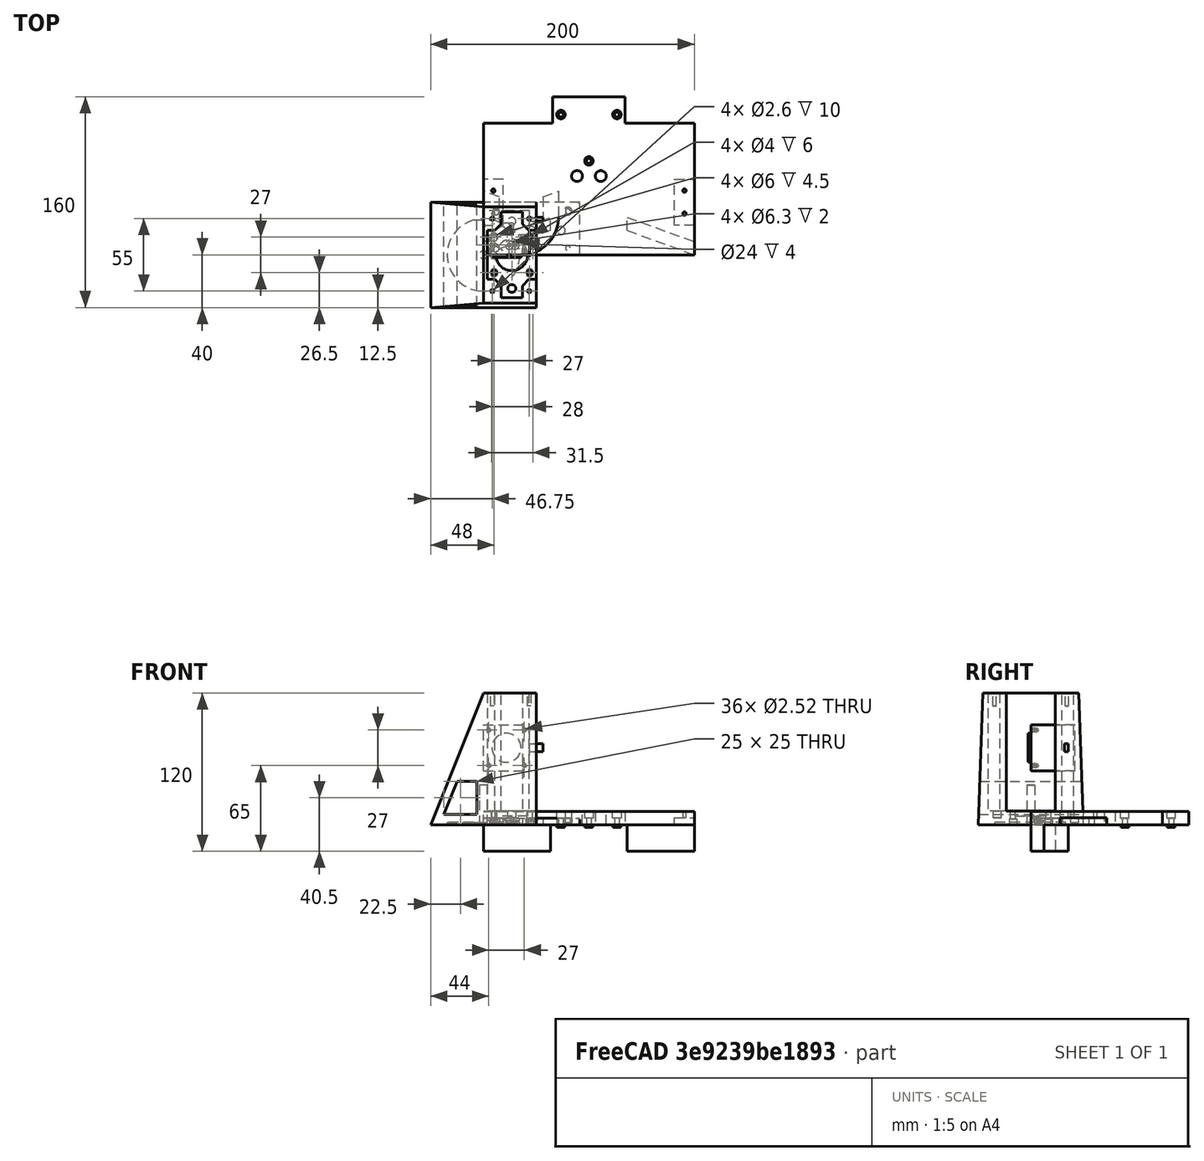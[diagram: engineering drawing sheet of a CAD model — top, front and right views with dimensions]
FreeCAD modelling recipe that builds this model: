
FCSTD DOCUMENT  (FreeCAD 1.0R39109 (Git))
Label: charging-station
License: All rights reserved
LicenseURL: http://en.wikipedia.org/wiki/All_rights_reserved
objects: Sketcher::SketchObject×37, PartDesign::Pocket×23, PartDesign::Pad×13, App::Link×9, App::FeaturePython×9, PartDesign::Body×8, PartDesign::Fillet×2, PartDesign::Hole×1, PartDesign::Chamfer×1, Assembly::JointGroup×1, Assembly::AssemblyObject×1
note: 202 computed .brp shape members not serialized (recipe doc carries the construction recipe); baked Part::Feature solids carry a one-line shape summary decoded from their .brp

FEATURE [Sketcher::SketchObject] Sketch
  ArcFitTolerance = 0
  AttachmentSupport = -> [XY_Plane]
  FullyConstrained = true
  MakeInternals = false
  MapMode = 5
  sketch-geometry (4):
    g0: LineSegment StartX=0 StartY=0 StartZ=0 EndX=160 EndY=0 EndZ=0
    g1: LineSegment StartX=160 StartY=0 StartZ=0 EndX=160 EndY=100 EndZ=0
    g2: LineSegment StartX=160 StartY=100 StartZ=0 EndX=0 EndY=100 EndZ=0
    g3: LineSegment StartX=0 StartY=100 StartZ=0 EndX=0 EndY=0 EndZ=0
  constraints (11):
    c: Coincident(g0,g1)
    c: Coincident(g1,g2)
    c: Coincident(g2,g3)
    c: Coincident(g3,g0)
    c: Horizontal(g0)
    c: Horizontal(g2)
    c: Vertical(g1)
    c: Vertical(g3)
    c: Coincident(g0,g-1)
    c: DistanceY(g1,g1) = 100
    c: DistanceX(g0,g0) = 160
FEATURE [PartDesign::Pad] Pad
  Direction = (0,0,1)
  Length = 10
  Length2 = 10
  Profile = -> Sketch
  ReferenceAxis = -> Sketch [N_Axis]
  Suppressed = false
  Type = 0
FEATURE [Sketcher::SketchObject] Sketch001
  ArcFitTolerance = 0
  AttachmentSupport = -> [Pad]
  ExternalGeometry = -> [Pad]
  FullyConstrained = true
  MakeInternals = false
  MapMode = 5
  Placement = pos=(0,0,0) rot=(1,0,0;3.14159rad)
  sketch-geometry (15):
    g0: LineSegment [constr] StartX=63.5 StartY=-33.1121 StartZ=0 EndX=96.5 EndY=-33.1121 EndZ=0
    g1: LineSegment StartX=0 StartY=-10 StartZ=0 EndX=0 EndY=0 EndZ=0
    g2: LineSegment [constr] StartX=63.5 StartY=-23.1121 StartZ=0 EndX=63.5 EndY=-33.1121 EndZ=0
    g3: LineSegment [constr] StartX=96.5 StartY=-33.1121 StartZ=0 EndX=96.5 EndY=-23.1121 EndZ=0
    g4: LineSegment StartX=160 StartY=0 StartZ=0 EndX=160 EndY=-10 EndZ=0
    g5: LineSegment StartX=51 StartY=-18.5625 StartZ=0 EndX=51 EndY=-28.5625 EndZ=0
    g6: LineSegment StartX=0 StartY=-10 StartZ=0 EndX=51 EndY=-28.5625 EndZ=0
    g7: LineSegment [constr] StartX=51 StartY=-28.5625 StartZ=0 EndX=63.5 EndY=-33.1121 EndZ=0
    g8: LineSegment [constr] StartX=63.5 StartY=-23.1121 StartZ=0 EndX=51 EndY=-18.5625 EndZ=0
    g9: LineSegment StartX=51 StartY=-18.5625 StartZ=0 EndX=0 EndY=0 EndZ=0
    g10: LineSegment StartX=109 StartY=-18.5625 StartZ=0 EndX=109 EndY=-28.5625 EndZ=0
    g11: LineSegment [constr] StartX=96.5 StartY=-23.1121 StartZ=0 EndX=109 EndY=-18.5625 EndZ=0
    g12: LineSegment StartX=109 StartY=-18.5625 StartZ=0 EndX=160 EndY=0 EndZ=0
    g13: LineSegment [constr] StartX=96.5 StartY=-33.1121 StartZ=0 EndX=109 EndY=-28.5625 EndZ=0
    g14: LineSegment StartX=109 StartY=-28.5625 StartZ=0 EndX=160 EndY=-10 EndZ=0
  constraints (40):
    c: DistanceX(g0,g0) = 33
    c: Horizontal(g0)
    c: Vertical(g3)
    c: Vertical(g4)
    c: Vertical(g2)
    c: Equal(g2,g3)
    c: DistanceY(g4,g4) = 10
    c: Coincident(g1,g-1)
    c: Vertical(g1)
    c: Vertical(g5)
    c: DistanceX(g5,g0) = 12.5
    c: Coincident(g1,g6)
    c: Coincident(g6,g5)
    c: Coincident(g6,g7)
    c: Coincident(g7,g2)
    c: Coincident(g2,g8)
    c: Coincident(g8,g5)
    c: Coincident(g8,g9)
    c: Coincident(g9,g1)
    c: Vertical(g10)
    c: Coincident(g3,g11)
    c: Coincident(g11,g10)
    c: Coincident(g11,g12)
    c: Coincident(g3,g13)
    c: Coincident(g13,g10)
    c: Coincident(g13,g14)
    c: Coincident(g14,g4)
    c: Equal(g13,g7)
    c: Coincident(g2,g0)
    c: Coincident(g3,g0)
    c: Parallel(g6,g9)
    c: Parallel(g14,g12)
    c: Parallel(g7,g8)
    c: Parallel(g13,g11)
    c: Parallel(g13,g14)
    c: Parallel(g7,g6)
    c: Angle(g-1,g12) = 0.349066
    c: Equal(g14,g6)
    c: Coincident(g12,g-3)
    c: Coincident(g4,g12)
FEATURE [Sketcher::SketchObject] Sketch002
  ArcFitTolerance = 0
  AttachmentSupport = -> [XY_Plane001]
  FullyConstrained = true
  MakeInternals = false
  MapMode = 5
  sketch-geometry (4):
    g0: LineSegment StartX=0 StartY=0 StartZ=0 EndX=35 EndY=0 EndZ=0
    g1: LineSegment StartX=35 StartY=0 StartZ=0 EndX=35 EndY=33.5 EndZ=0
    g2: LineSegment StartX=35 StartY=33.5 StartZ=0 EndX=0 EndY=33.5 EndZ=0
    g3: LineSegment StartX=0 StartY=33.5 StartZ=0 EndX=0 EndY=0 EndZ=0
  constraints (11):
    c: Coincident(g0,g1)
    c: Coincident(g1,g2)
    c: Coincident(g2,g3)
    c: Coincident(g3,g0)
    c: Horizontal(g0)
    c: Horizontal(g2)
    c: Vertical(g1)
    c: Vertical(g3)
    c: Coincident(g0,g-1)
    c: DistanceY(g1,g1) = 33.5
    c: DistanceX(g2,g2) = 35
FEATURE [PartDesign::Pad] Pad001
  Direction = (0,0,1)
  Length = 35
  Length2 = 10
  Profile = -> Sketch002
  ReferenceAxis = -> Sketch002 [N_Axis]
  Refine = true
  Suppressed = false
  Type = 0
FEATURE [Sketcher::SketchObject] Sketch003
  ArcFitTolerance = 0
  AttachmentSupport = -> [Pad001]
  ExternalGeometry = -> [Pad001]
  FullyConstrained = true
  MakeInternals = false
  MapMode = 5
  Placement = pos=(0,0,0) rot=(1,0,0;1.5708rad)
  sketch-geometry (4):
    g0: LineSegment [constr] StartX=0 StartY=0 StartZ=0 EndX=35 EndY=35 EndZ=0
    g1: LineSegment [constr] StartX=0 StartY=35 StartZ=0 EndX=35 EndY=0 EndZ=0
    g2: GeomPoint [constr] X=17.5 Y=17.5 Z=0
    g3: Circle CenterX=17.5 CenterY=17.5 CenterZ=0 NormalX=0 NormalY=0 NormalZ=1 AngleXU=0 Radius=11
  constraints (7):
    c: Coincident(g-1,g0)
    c: Coincident(g0,g-3)
    c: Coincident(g1,g-4)
    c: Coincident(g1,g-5)
    c: Symmetric(g1,g1,g2)
    c: Coincident(g3,g2)
    c: Diameter(g3) = 22
FEATURE [PartDesign::Pad] Pad002
  BaseFeature = -> Pad001
  Direction = (0,-1,2e-16)
  Length = 2
  Length2 = 10
  Profile = -> Sketch003
  ReferenceAxis = -> Sketch003 [N_Axis]
  Refine = true
  Suppressed = false
  Type = 0
FEATURE [Sketcher::SketchObject] Sketch004
  ArcFitTolerance = 0
  AttachmentSupport = -> [Pad002]
  ExternalGeometry = -> [Pad002]
  FullyConstrained = true
  MakeInternals = false
  MapMode = 5
  Placement = pos=(0,0,0) rot=(1,0,0;1.5708rad)
  sketch-geometry (6):
    g0: LineSegment [constr] StartX=35 StartY=35 StartZ=0 EndX=0 EndY=0 EndZ=0
    g1: LineSegment [constr] StartX=0 StartY=35 StartZ=0 EndX=35 EndY=0 EndZ=0
    g2: Circle CenterX=31 CenterY=31 CenterZ=0 NormalX=0 NormalY=0 NormalZ=1 AngleXU=0 Radius=1.5
    g3: Circle CenterX=4 CenterY=31 CenterZ=0 NormalX=0 NormalY=0 NormalZ=1 AngleXU=0 Radius=1.5
    g4: Circle CenterX=31 CenterY=4 CenterZ=0 NormalX=0 NormalY=0 NormalZ=1 AngleXU=0 Radius=1.5
    g5: Circle CenterX=4 CenterY=4 CenterZ=0 NormalX=0 NormalY=0 NormalZ=1 AngleXU=0 Radius=1.5
  constraints (16):
    c: Coincident(g-7,g0)
    c: Coincident(g0,g-1)
    c: Coincident(g-9,g1)
    c: Coincident(g1,g-8)
    c: PointOnObject(g2,g0)
    c: PointOnObject(g3,g1)
    c: PointOnObject(g4,g1)
    c: PointOnObject(g5,g0)
    c: DistanceX(g2,g0) = 4
    c: DistanceX(g4,g1) = 4
    c: DistanceX(g0,g5) = 4
    c: DistanceX(g1,g3) = 4
    c: Diameter(g2) = 3
    c: Diameter(g4) = 3
    c: Diameter(g5) = 3
    c: Diameter(g3) = 3
FEATURE [PartDesign::Hole] Hole
  BaseFeature = -> Pad002
  CustomThreadClearance = 0
  Depth = 5
  DepthType = 0
  Diameter = 2.52
  DrillForDepth = false
  DrillPoint = 1
  DrillPointAngle = 118
  HoleCutCountersinkAngle = 90
  HoleCutCustomValues = false
  HoleCutDepth = 0
  HoleCutDiameter = 6
  HoleCutType = 0
  ModelThread = true
  Profile = -> Sketch004
  Refine = true
  Suppressed = false
  Tapered = false
  TaperedAngle = 90
  ThreadClass = 0
  ThreadDepth = 5
  ThreadDepthType = 0
  ThreadDirection = 0
  ThreadFit = 0
  ThreadSize = 9
  ThreadType = 1
  Threaded = true
  UseCustomThreadClearance = false
FEATURE [Sketcher::SketchObject] Sketch005
  ArcFitTolerance = 0
  AttachmentSupport = -> [Hole]
  ExternalGeometry = -> [Hole]
  FullyConstrained = true
  MakeInternals = false
  MapMode = 5
  Placement = pos=(35,0,0) rot=(0.57735,0.57735,0.57735;2.0944rad)
  sketch-geometry (9):
    g0: LineSegment [constr] StartX=33.5 StartY=35 StartZ=0 EndX=33.5 EndY=20.5 EndZ=0
    g1: LineSegment [constr] StartX=33.5 StartY=20.5 StartZ=0 EndX=33.5 EndY=14.5 EndZ=0
    g2: LineSegment [constr] StartX=33.5 StartY=14.5 StartZ=0 EndX=33.5 EndY=0 EndZ=0
    g3: LineSegment [constr] StartX=33.5 StartY=20.5 StartZ=0 EndX=28.5 EndY=20.5 EndZ=0
    g4: LineSegment [constr] StartX=33.5 StartY=14.5 StartZ=0 EndX=28.5 EndY=14.5 EndZ=0
    g5: LineSegment StartX=28.5 StartY=20.5 StartZ=0 EndX=25.5 EndY=20.5 EndZ=0
    g6: LineSegment StartX=25.5 StartY=20.5 StartZ=0 EndX=25.5 EndY=14.5 EndZ=0
    g7: LineSegment StartX=25.5 StartY=14.5 StartZ=0 EndX=28.5 EndY=14.5 EndZ=0
    g8: LineSegment StartX=28.5 StartY=14.5 StartZ=0 EndX=28.5 EndY=20.5 EndZ=0
  constraints (24):
    c: Coincident(g-4,g0)
    c: PointOnObject(g0,g-3)
    c: Coincident(g0,g1)
    c: PointOnObject(g1,g-3)
    c: Coincident(g1,g2)
    c: Coincident(g2,g-3)
    c: Equal(g2,g0)
    c: DistanceY(g1,g1) = 6
    c: Coincident(g0,g3)
    c: Horizontal(g3)
    c: Coincident(g1,g4)
    c: Horizontal(g4)
    c: Coincident(g5,g6)
    c: Coincident(g6,g7)
    c: Coincident(g7,g8)
    c: Coincident(g8,g5)
    c: Horizontal(g5)
    c: Horizontal(g7)
    c: Vertical(g6)
    c: Vertical(g8)
    c: Coincident(g5,g3)
    c: Coincident(g7,g4)
    c: DistanceX(g5,g5) = 3
    c: DistanceX(g3,g3) = 5
FEATURE [Sketcher::SketchObject] Sketch006
  ArcFitTolerance = 0
  AttachmentSupport = -> [XY_Plane002]
  FullyConstrained = true
  MakeInternals = false
  MapMode = 5
  sketch-geometry (2):
    g0: ArcOfCircle CenterX=0 CenterY=0 CenterZ=0 NormalX=0 NormalY=0 NormalZ=1 AngleXU=0 Radius=27.5 StartAngle=1.8413 EndAngle=7.58348
    g1: LineSegment StartX=-7.34847 StartY=26.5 StartZ=0 EndX=7.34847 EndY=26.5 EndZ=0
  constraints (6):
    c: Coincident(g0,g-1)
    c: Diameter(g0) = 55
    c: Horizontal(g1)
    c: Distance(g0,g1) = 26.5
    c: Coincident(g0,g1)
    c: Coincident(g0,g1)
FEATURE [PartDesign::Pad] Pad004
  Direction = (0,0,1)
  Length = 2
  Length2 = 10
  Profile = -> Sketch006
  ReferenceAxis = -> Sketch006 [N_Axis]
  Refine = true
  Suppressed = false
  Type = 0
FEATURE [PartDesign::Body] Body002  label="dezibot"
  AllowCompound = false
  Group = -> [Sketch006,Pad004]
  Origin = -> Origin002
  Tip = -> Pad004
FEATURE [App::Link] Body003  label="Beam"
  LinkPlacement = pos=(-173.162,-33.5765,-80.1161) rot=(0,0,1;0rad)
  LinkedObject = -> Body
  Placement = pos=(-173.162,-33.5765,-80.1161) rot=(0,0,1;0rad)
FEATURE [App::Link] Body004  label="BaseLeft"
  LinkPlacement = pos=(-213.899,29.7686,-94.7418) rot=(0,0,1;0rad)
  LinkedObject = -> Body006
  Placement = pos=(-213.899,29.7686,-94.7418) rot=(0,0,1;0rad)
FEATURE [Sketcher::SketchObject] Sketch007
  ArcFitTolerance = 0
  AttachmentSupport = -> [XY_Plane004]
  FullyConstrained = true
  MakeInternals = false
  MapMode = 5
  sketch-geometry (8):
    g0: LineSegment StartX=-40 StartY=40 StartZ=0 EndX=-40 EndY=-40 EndZ=0
    g1: LineSegment StartX=-40 StartY=-40 StartZ=0 EndX=40 EndY=-40 EndZ=0
    g2: LineSegment StartX=40 StartY=-40 StartZ=0 EndX=40 EndY=40 EndZ=0
    g3: LineSegment StartX=40 StartY=40 StartZ=0 EndX=-40 EndY=40 EndZ=0
    g4: LineSegment [constr] StartX=40 StartY=-40 StartZ=0 EndX=0 EndY=0 EndZ=0
    g5: LineSegment [constr] StartX=0 StartY=0 StartZ=0 EndX=-40 EndY=40 EndZ=0
    g6: LineSegment [constr] StartX=-40 StartY=-40 StartZ=0 EndX=0 EndY=0 EndZ=0
    g7: LineSegment [constr] StartX=0 StartY=0 StartZ=0 EndX=40 EndY=40 EndZ=0
  constraints (20):
    c: Coincident(g0,g1)
    c: Coincident(g1,g2)
    c: Coincident(g2,g3)
    c: Coincident(g3,g0)
    c: Vertical(g0)
    c: Vertical(g2)
    c: Horizontal(g1)
    c: Horizontal(g3)
    c: DistanceY(g2,g2) = 80
    c: DistanceX(g1,g1) = 80
    c: Coincident(g1,g4)
    c: Coincident(g4,g-1)
    c: Coincident(g4,g5)
    c: Coincident(g5,g0)
    c: Equal(g5,g4)
    c: Coincident(g0,g6)
    c: Coincident(g6,g4)
    c: Coincident(g6,g7)
    c: Coincident(g7,g2)
    c: Equal(g7,g6)
FEATURE [PartDesign::Pad] Pad005
  Direction = (0,0,1)
  Length = 100
  Length2 = 10
  Profile = -> Sketch007
  ReferenceAxis = -> Sketch007 [N_Axis]
  Refine = true
  Suppressed = false
  Type = 0
FEATURE [Sketcher::SketchObject] Sketch008
  ArcFitTolerance = 0
  AttachmentSupport = -> [Pad005]
  ExternalGeometry = -> [Pad005]
  FullyConstrained = true
  MakeInternals = false
  MapMode = 5
  Placement = pos=(0,-40,0) rot=(1,0,0;1.5708rad)
  sketch-geometry (10):
    g0: LineSegment StartX=-40 StartY=0 StartZ=0 EndX=0 EndY=100 EndZ=0
    g1: LineSegment [constr] StartX=0 StartY=100 StartZ=0 EndX=40 EndY=100 EndZ=0
    g2: LineSegment [constr] StartX=40 StartY=100 StartZ=0 EndX=40 EndY=0 EndZ=0
    g3: LineSegment [constr] StartX=40 StartY=0 StartZ=0 EndX=-40 EndY=0 EndZ=0
    g4: LineSegment StartX=0 StartY=100 StartZ=0 EndX=-40 EndY=100 EndZ=0
    g5: LineSegment StartX=-40 StartY=100 StartZ=0 EndX=-40 EndY=0 EndZ=0
    g6: LineSegment StartX=-30 StartY=8 StartZ=0 EndX=-5 EndY=8 EndZ=0
    g7: LineSegment StartX=-5 StartY=8 StartZ=0 EndX=-5 EndY=33 EndZ=0
    g8: LineSegment StartX=-20 StartY=33 StartZ=0 EndX=-30 EndY=8 EndZ=0
    g9: LineSegment StartX=-5 StartY=33 StartZ=0 EndX=-20 EndY=33 EndZ=0
  constraints (26):
    c: Coincident(g-4,g0)
    c: Coincident(g0,g1)
    c: Coincident(g1,g-5)
    c: Horizontal(g1)
    c: Coincident(g1,g2)
    c: Coincident(g2,g-5)
    c: Coincident(g2,g3)
    c: Coincident(g3,g0)
    c: DistanceX(g1,g1) = 40
    c: Coincident(g0,g4)
    c: Horizontal(g4)
    c: Coincident(g4,g5)
    c: Coincident(g5,g0)
    c: Vertical(g5)
    c: Horizontal(g6)
    c: Coincident(g6,g7)
    c: Vertical(g7)
    c: Coincident(g8,g6)
    c: DistanceX(g6,g-1) = 5
    c: DistanceY(g-1,g6) = 8
    c: DistanceX(g0,g6) = 10
    c: Parallel(g8,g0)
    c: Horizontal(g9)
    c: DistanceY(g6,g9) = 25
    c: Coincident(g7,g9)
    c: Coincident(g8,g9)
FEATURE [PartDesign::Pocket] Pocket001
  BaseFeature = -> Pad005
  Direction = (0,1,-2e-16)
  Length = 5
  Length2 = 5
  Profile = -> Sketch008
  ReferenceAxis = -> Sketch008 [N_Axis]
  Refine = true
  Suppressed = false
  Type = 1
FEATURE [Sketcher::SketchObject] Sketch009
  ArcFitTolerance = 0
  AttachmentSupport = -> [Pocket001]
  ExternalGeometry = -> [Pocket001]
  FullyConstrained = true
  MakeInternals = false
  MapMode = 5
  Placement = pos=(40,0,0) rot=(0.57735,0.57735,0.57735;2.0944rad)
  sketch-geometry (6):
    g0: LineSegment StartX=-36.5 StartY=100 StartZ=0 EndX=-40 EndY=0 EndZ=0
    g1: LineSegment StartX=40 StartY=0 StartZ=0 EndX=36.5 EndY=100 EndZ=0
    g2: LineSegment StartX=-36.5 StartY=100 StartZ=0 EndX=-40 EndY=100 EndZ=0
    g3: LineSegment StartX=-40 StartY=100 StartZ=0 EndX=-40 EndY=0 EndZ=0
    g4: LineSegment StartX=36.5 StartY=100 StartZ=0 EndX=40 EndY=100 EndZ=0
    g5: LineSegment StartX=40 StartY=100 StartZ=0 EndX=40 EndY=0 EndZ=0
  constraints (13):
    c: DistanceX(g0,g1) = 73
    c: Symmetric(g0,g1,g-2)
    c: Coincident(g-3,g1)
    c: PointOnObject(g1,g-4)
    c: Coincident(g0,g-3)
    c: Coincident(g0,g2)
    c: Coincident(g2,g-4)
    c: Coincident(g2,g3)
    c: Coincident(g3,g0)
    c: Coincident(g1,g4)
    c: Coincident(g4,g-4)
    c: Coincident(g4,g5)
    c: Coincident(g5,g1)
FEATURE [PartDesign::Pocket] Pocket002
  BaseFeature = -> Pocket001
  Direction = (-1,0,0)
  Length = 5
  Length2 = 5
  Profile = -> Sketch009
  ReferenceAxis = -> Sketch009 [N_Axis]
  Refine = true
  Suppressed = false
  Type = 1
FEATURE [App::FeaturePython] GroundedJoint001  # Assembly grounded joint (typed FeaturePython)
  ObjectToGround = -> Body004
  Placement = pos=(-213.899,29.7686,-94.7418) rot=(0,0,1;0rad)
FEATURE [Sketcher::SketchObject] Sketch011
  ArcFitTolerance = 0
  AttachmentSupport = -> [Pocket002]
  ExternalGeometry = -> [Pocket002]
  FullyConstrained = true
  MakeInternals = false
  MapMode = 5
  Placement = pos=(40,0,0) rot=(0.57735,0.57735,0.57735;2.0944rad)
  sketch-geometry (5):
    g0: LineSegment StartX=-18.5 StartY=10.5 StartZ=0 EndX=18.5 EndY=10.5 EndZ=0
    g1: LineSegment StartX=18.5 StartY=10.5 StartZ=0 EndX=18.5 EndY=1671.43 EndZ=0
    g2: LineSegment StartX=18.5 StartY=1671.43 StartZ=0 EndX=-18.5 EndY=1671.43 EndZ=0
    g3: LineSegment StartX=-18.5 StartY=1671.43 StartZ=0 EndX=-18.5 EndY=10.5 EndZ=0
    g4: GeomPoint X=0 Y=1671.43 Z=0
  constraints (13):
    c: Coincident(g0,g1)
    c: Coincident(g1,g2)
    c: Coincident(g2,g3)
    c: Coincident(g3,g0)
    c: Horizontal(g0)
    c: Horizontal(g2)
    c: Vertical(g1)
    c: Vertical(g3)
    c: PointOnObject(g1,g-3)
    c: DistanceX(g2,g2) = 37
    c: Symmetric(g2,g2,g4)
    c: PointOnObject(g4,g-2)
    c: DistanceY(g-1,g0) = 10.5
FEATURE [PartDesign::Pocket] Pocket003
  BaseFeature = -> Pocket002
  Direction = (-1,0,0)
  Length = 37
  Length2 = 5
  Profile = -> Sketch011
  ReferenceAxis = -> Sketch011 [N_Axis]
  Refine = true
  Suppressed = false
  Type = 0
FEATURE [Sketcher::SketchObject] Sketch012
  ArcFitTolerance = 0
  AttachmentSupport = -> [Pocket003]
  ExternalGeometry = -> [Pocket003]
  FullyConstrained = true
  MakeInternals = false
  MapMode = 5
  Placement = pos=(0,0,10.5) rot=(0,0,1;0rad)
  sketch-geometry (4):
    g0: Circle CenterX=21.5 CenterY=0 CenterZ=0 NormalX=0 NormalY=0 NormalZ=1 AngleXU=0 Radius=12
    g1: LineSegment [constr] StartX=3 StartY=18.5 StartZ=0 EndX=40 EndY=-18.5 EndZ=0
    g2: LineSegment [constr] StartX=40 StartY=18.5 StartZ=0 EndX=3 EndY=-18.5 EndZ=0
    g3: GeomPoint [constr] X=21.5 Y=0 Z=0
  constraints (7):
    c: Diameter(g0) = 24
    c: Coincident(g1,g-3)
    c: Coincident(g1,g-5)
    c: Coincident(g2,g-6)
    c: Coincident(g2,g-4)
    c: Symmetric(g1,g1,g3)
    c: Coincident(g3,g0)
FEATURE [PartDesign::Pocket] Pocket004
  BaseFeature = -> Pocket003
  Direction = (0,0,-1)
  Length = 4
  Length2 = 5
  Profile = -> Sketch012
  ReferenceAxis = -> Sketch012 [N_Axis]
  Refine = true
  Suppressed = false
  Type = 0
FEATURE [Sketcher::SketchObject] Sketch013
  ArcFitTolerance = 0
  AttachmentSupport = -> [Pocket004]
  ExternalGeometry = -> [Pocket004]
  FullyConstrained = true
  MakeInternals = false
  MapMode = 5
  Placement = pos=(0,0,10.5) rot=(0,0,1;0rad)
  sketch-geometry (20):
    g0: LineSegment [constr] StartX=3 StartY=18.5 StartZ=0 EndX=3 EndY=13.5 EndZ=0
    g1: LineSegment [constr] StartX=3 StartY=13.5 StartZ=0 EndX=8 EndY=13.5 EndZ=0
    g2: LineSegment [constr] StartX=8 StartY=13.5 StartZ=0 EndX=8 EndY=18.5 EndZ=0
    g3: LineSegment [constr] StartX=8 StartY=18.5 StartZ=0 EndX=3 EndY=18.5 EndZ=0
    g4: LineSegment [constr] StartX=35 StartY=13.5 StartZ=0 EndX=40 EndY=13.5 EndZ=0
    g5: LineSegment [constr] StartX=40 StartY=13.5 StartZ=0 EndX=40 EndY=18.5 EndZ=0
    g6: LineSegment [constr] StartX=40 StartY=18.5 StartZ=0 EndX=35 EndY=18.5 EndZ=0
    g7: LineSegment [constr] StartX=35 StartY=18.5 StartZ=0 EndX=35 EndY=13.5 EndZ=0
    g8: LineSegment [constr] StartX=3 StartY=-18.5 StartZ=0 EndX=8 EndY=-18.5 EndZ=0
    g9: LineSegment [constr] StartX=8 StartY=-18.5 StartZ=0 EndX=8 EndY=-13.5 EndZ=0
    g10: LineSegment [constr] StartX=8 StartY=-13.5 StartZ=0 EndX=3 EndY=-13.5 EndZ=0
    g11: LineSegment [constr] StartX=3 StartY=-13.5 StartZ=0 EndX=3 EndY=-18.5 EndZ=0
    g12: LineSegment [constr] StartX=35 StartY=-13.5 StartZ=0 EndX=35 EndY=-18.5 EndZ=0
    g13: LineSegment [constr] StartX=35 StartY=-18.5 StartZ=0 EndX=40 EndY=-18.5 EndZ=0
    g14: LineSegment [constr] StartX=40 StartY=-18.5 StartZ=0 EndX=40 EndY=-13.5 EndZ=0
    g15: LineSegment [constr] StartX=40 StartY=-13.5 StartZ=0 EndX=35 EndY=-13.5 EndZ=0
    g16: Circle CenterX=8 CenterY=13.5 CenterZ=0 NormalX=0 NormalY=0 NormalZ=1 AngleXU=0 Radius=2
    g17: Circle CenterX=35 CenterY=13.5 CenterZ=0 NormalX=0 NormalY=0 NormalZ=1 AngleXU=0 Radius=2
    g18: Circle CenterX=35 CenterY=-13.5 CenterZ=0 NormalX=0 NormalY=0 NormalZ=1 AngleXU=0 Radius=2
    g19: Circle CenterX=8 CenterY=-13.5 CenterZ=0 NormalX=0 NormalY=0 NormalZ=1 AngleXU=0 Radius=2
  constraints (52):
    c: Coincident(g0,g1)
    c: Coincident(g1,g2)
    c: Coincident(g2,g3)
    c: Coincident(g3,g0)
    c: Vertical(g0)
    c: Vertical(g2)
    c: Horizontal(g1)
    c: Horizontal(g3)
    c: Coincident(g0,g-4)
    c: Equal(g2,g1)
    c: DistanceY(g2,g2) = 5
    c: Coincident(g4,g5)
    c: Coincident(g5,g6)
    c: Coincident(g6,g7)
    c: Coincident(g7,g4)
    c: Horizontal(g4)
    c: Horizontal(g6)
    c: Vertical(g5)
    c: Vertical(g7)
    c: Coincident(g8,g9)
    c: Coincident(g9,g10)
    c: Coincident(g10,g11)
    c: Coincident(g11,g8)
    c: Horizontal(g8)
    c: Horizontal(g10)
    c: Vertical(g9)
    c: Vertical(g11)
    c: Coincident(g12,g13)
    c: Coincident(g13,g14)
    c: Coincident(g14,g15)
    c: Coincident(g15,g12)
    c: Vertical(g12)
    c: Vertical(g14)
    c: Horizontal(g13)
    c: Horizontal(g15)
    c: Equal(g7,g2)
    c: Equal(g4,g2)
    c: Coincident(g5,g-6)
    c: Coincident(g8,g-5)
    c: Equal(g10,g1)
    c: Equal(g10,g9)
    c: Equal(g12,g2)
    c: Equal(g15,g1)
    c: Coincident(g13,g-6)
    c: Coincident(g16,g1)
    c: Diameter(g16) = 4
    c: Coincident(g17,g4)
    c: Coincident(g18,g12)
    c: Coincident(g19,g9)
    c: Equal(g16,g17)
    c: Equal(g17,g18)
    c: Equal(g18,g19)
FEATURE [PartDesign::Pocket] Pocket005
  BaseFeature = -> Pocket004
  Direction = (0,0,-1)
  Length = 5
  Length2 = 5
  Profile = -> Sketch013
  ReferenceAxis = -> Sketch013 [N_Axis]
  Refine = true
  Suppressed = false
  Type = 1
FEATURE [Sketcher::SketchObject] Sketch014
  ArcFitTolerance = 0
  AttachmentSupport = -> [Pocket005]
  ExternalGeometry = -> [Pocket005]
  FullyConstrained = true
  MakeInternals = false
  MapMode = 5
  Placement = pos=(0,0,0) rot=(1,0,0;3.14159rad)
  sketch-geometry (4):
    g0: Circle CenterX=8 CenterY=13.5 CenterZ=0 NormalX=0 NormalY=0 NormalZ=1 AngleXU=0 Radius=3
    g1: Circle CenterX=35 CenterY=13.5 CenterZ=0 NormalX=0 NormalY=0 NormalZ=1 AngleXU=0 Radius=3
    g2: Circle CenterX=35 CenterY=-13.5 CenterZ=0 NormalX=0 NormalY=0 NormalZ=1 AngleXU=0 Radius=3
    g3: Circle CenterX=8 CenterY=-13.5 CenterZ=0 NormalX=0 NormalY=0 NormalZ=1 AngleXU=0 Radius=3
  constraints (8):
    c: Coincident(g0,g-3)
    c: Coincident(g1,g-4)
    c: Coincident(g2,g-5)
    c: Coincident(g3,g-6)
    c: Diameter(g0) = 6
    c: Equal(g0,g1)
    c: Equal(g1,g2)
    c: Equal(g2,g3)
FEATURE [App::Link] Body005  label="BaseRight"
  LinkPlacement = pos=(67.4324,29.1063,-94.7418) rot=(0,0,1;3.14159rad)
  LinkedObject = -> Body006
  Placement = pos=(67.4324,29.1063,-94.7418) rot=(0,0,1;3.14159rad)
FEATURE [App::FeaturePython] GroundedJoint  # Assembly grounded joint (typed FeaturePython)
  ObjectToGround = -> Body005
  Placement = pos=(67.4324,29.1063,-94.7418) rot=(0,0,1;3.14159rad)
FEATURE [Sketcher::SketchObject] Sketch019
  ArcFitTolerance = 0
  AttachmentSupport = -> [XY_Plane005]
  FullyConstrained = true
  MakeInternals = false
  MapMode = 5
  sketch-geometry (4):
    g0: LineSegment StartX=0 StartY=0 StartZ=0 EndX=73 EndY=0 EndZ=0
    g1: LineSegment StartX=73 StartY=0 StartZ=0 EndX=73 EndY=40 EndZ=0
    g2: LineSegment StartX=73 StartY=40 StartZ=0 EndX=0 EndY=40 EndZ=0
    g3: LineSegment StartX=0 StartY=40 StartZ=0 EndX=0 EndY=0 EndZ=0
  constraints (11):
    c: Coincident(g0,g1)
    c: Coincident(g1,g2)
    c: Coincident(g2,g3)
    c: Coincident(g3,g0)
    c: Horizontal(g0)
    c: Horizontal(g2)
    c: Vertical(g1)
    c: Vertical(g3)
    c: Coincident(g0,g-1)
    c: DistanceY(g1,g1) = 40
    c: DistanceX(g2,g2) = 73
FEATURE [PartDesign::Pad] Pad006
  Direction = (0,0,1)
  Length = 5
  Length2 = 10
  Profile = -> Sketch019
  ReferenceAxis = -> Sketch019 [N_Axis]
  Refine = true
  Suppressed = false
  Type = 0
FEATURE [Sketcher::SketchObject] Sketch020
  ArcFitTolerance = 0
  AttachmentSupport = -> [Pad006]
  ExternalGeometry = -> [Pad006]
  FullyConstrained = true
  MakeInternals = false
  MapMode = 5
  Placement = pos=(0,0,5) rot=(0,0,1;0rad)
  sketch-geometry (35):
    g0: LineSegment [constr] StartX=0 StartY=0 StartZ=0 EndX=18 EndY=0 EndZ=0
    g1: LineSegment [constr] StartX=18 StartY=0 StartZ=0 EndX=18 EndY=10.5 EndZ=0
    g2: LineSegment [constr] StartX=18 StartY=10.5 StartZ=0 EndX=0 EndY=10.5 EndZ=0
    g3: LineSegment [constr] StartX=0 StartY=10.5 StartZ=0 EndX=0 EndY=0 EndZ=0
    g4: LineSegment [constr] StartX=0 StartY=40 StartZ=0 EndX=0 EndY=26.5 EndZ=0
    g5: LineSegment [constr] StartX=0 StartY=26.5 StartZ=0 EndX=18 EndY=26.5 EndZ=0
    g6: LineSegment [constr] StartX=18 StartY=26.5 StartZ=0 EndX=18 EndY=37 EndZ=0
    g7: LineSegment [constr] StartX=18 StartY=40 StartZ=0 EndX=0 EndY=40 EndZ=0
    g8: LineSegment [constr] StartX=73 StartY=40 StartZ=0 EndX=55 EndY=40 EndZ=0
    g9: LineSegment [constr] StartX=55 StartY=37 StartZ=0 EndX=55 EndY=26.5 EndZ=0
    g10: LineSegment [constr] StartX=55 StartY=26.5 StartZ=0 EndX=73 EndY=26.5 EndZ=0
    g11: LineSegment [constr] StartX=73 StartY=26.5 StartZ=0 EndX=73 EndY=40 EndZ=0
    g12: LineSegment [constr] StartX=73 StartY=0 StartZ=0 EndX=73 EndY=10.5 EndZ=0
    g13: LineSegment [constr] StartX=73 StartY=10.5 StartZ=0 EndX=55 EndY=10.5 EndZ=0
    g14: LineSegment [constr] StartX=55 StartY=10.5 StartZ=0 EndX=55 EndY=0 EndZ=0
    g15: LineSegment [constr] StartX=55 StartY=0 StartZ=0 EndX=73 EndY=0 EndZ=0
    g16: Circle CenterX=14 CenterY=18.5 CenterZ=0 NormalX=0 NormalY=0 NormalZ=1 AngleXU=0 Radius=3
    g17: Circle CenterX=59 CenterY=18.5 CenterZ=0 NormalX=0 NormalY=0 NormalZ=1 AngleXU=0 Radius=3
    g18: Circle CenterX=36.5 CenterY=18.5 CenterZ=0 NormalX=0 NormalY=0 NormalZ=1 AngleXU=0 Radius=3
    g19: Circle CenterX=9 CenterY=33.25 CenterZ=0 NormalX=0 NormalY=0 NormalZ=1 AngleXU=0 Radius=1.75
    g20: Circle CenterX=64 CenterY=33.25 CenterZ=0 NormalX=0 NormalY=0 NormalZ=1 AngleXU=0 Radius=1.75
    g21: Circle CenterX=64 CenterY=5.25 CenterZ=0 NormalX=0 NormalY=0 NormalZ=1 AngleXU=0 Radius=1.75
    g22: Circle CenterX=9 CenterY=5.25 CenterZ=0 NormalX=0 NormalY=0 NormalZ=1 AngleXU=0 Radius=1.75
    g23: LineSegment [constr] StartX=0 StartY=26.5 StartZ=0 EndX=0 EndY=10.5 EndZ=0
    g24: LineSegment [constr] StartX=0 StartY=10.5 StartZ=0 EndX=10 EndY=10.5 EndZ=0
    g25: LineSegment [constr] StartX=10 StartY=10.5 StartZ=0 EndX=10 EndY=26.5 EndZ=0
    g26: LineSegment [constr] StartX=10 StartY=26.5 StartZ=0 EndX=0 EndY=26.5 EndZ=0
    g27: LineSegment [constr] StartX=73 StartY=10.5 StartZ=0 EndX=73 EndY=26.5 EndZ=0
    g28: LineSegment [constr] StartX=73 StartY=26.5 StartZ=0 EndX=63 EndY=26.5 EndZ=0
    g29: LineSegment [constr] StartX=63 StartY=26.5 StartZ=0 EndX=63 EndY=10.5 EndZ=0
    g30: LineSegment [constr] StartX=63 StartY=10.5 StartZ=0 EndX=73 EndY=10.5 EndZ=0
    g31: LineSegment [constr] StartX=18 StartY=40 StartZ=0 EndX=18 EndY=37 EndZ=0
    g32: LineSegment [constr] StartX=18 StartY=37 StartZ=0 EndX=55 EndY=37 EndZ=0
    g33: LineSegment [constr] StartX=55 StartY=37 StartZ=0 EndX=55 EndY=40 EndZ=0
    g34: LineSegment [constr] StartX=55 StartY=40 StartZ=0 EndX=18 EndY=40 EndZ=0
  constraints (92):
    c: Coincident(g0,g1)
    c: Coincident(g1,g2)
    c: Coincident(g2,g3)
    c: Coincident(g3,g0)
    c: Horizontal(g0)
    c: Horizontal(g2)
    c: Vertical(g1)
    c: Vertical(g3)
    c: Coincident(g0,g-1)
    c: Coincident(g4,g5)
    c: Coincident(g5,g6)
    c: Vertical(g4)
    c: Vertical(g6)
    c: Horizontal(g5)
    c: Horizontal(g7)
    c: Coincident(g9,g10)
    c: Coincident(g10,g11)
    c: Coincident(g11,g8)
    c: Horizontal(g8)
    c: Horizontal(g10)
    c: Vertical(g9)
    c: Vertical(g11)
    c: Coincident(g8,g-5)
    c: Coincident(g12,g13)
    c: Coincident(g13,g14)
    c: Coincident(g14,g15)
    c: Coincident(g15,g12)
    c: Vertical(g12)
    c: Vertical(g14)
    c: Horizontal(g13)
    c: Horizontal(g15)
    c: Coincident(g12,g-6)
    c: DistanceY(g2,g4) = 16
    c: DistanceX(g-1,g0) = 18
    c: Symmetric(g25,g1,g16)
    c: Symmetric(g9,g29,g17)
    c: Symmetric(g5,g13,g18)
    c: Diameter(g18) = 6
    c: Diameter(g16) = 6
    c: Equal(g16,g17)
    c: Symmetric(g13,g12,g21)
    c: Diameter(g19) = 3.5
    c: Coincident(g23,g24)
    c: Coincident(g24,g25)
    c: Coincident(g25,g26)
    c: Coincident(g26,g23)
    c: Vertical(g23)
    c: Vertical(g25)
    c: Horizontal(g24)
    c: Horizontal(g26)
    c: Coincident(g23,g4)
    c: PointOnObject(g24,g2)
    c: DistanceX(g24,g1) = 8
    c: Coincident(g27,g28)
    c: Coincident(g28,g29)
    c: Coincident(g29,g30)
    c: Coincident(g30,g27)
    c: Vertical(g27)
    c: Vertical(g29)
    c: Horizontal(g28)
    c: Horizontal(g30)
    c: Coincident(g27,g12)
    c: PointOnObject(g28,g10)
    c: DistanceX(g13,g29) = 8
    c: Coincident(g31,g32)
    c: Coincident(g32,g33)
    c: Coincident(g33,g34)
    c: Coincident(g34,g31)
    c: Vertical(g31)
    c: Vertical(g33)
    c: Horizontal(g32)
    c: Coincident(g31,g7)
    c: Coincident(g-4,g7)
    c: Coincident(g4,g7)
    c: Distance(g32,g8) = 3
    c: DistanceY(g5,g31) = 10.5
    c: DistanceY(g5,g7) = 13.5
    c: Symmetric(g5,g4,g19)
    c: Symmetric(g0,g1,g22)
    c: Symmetric(g9,g8,g20)
    c: Equal(g19,g22)
    c: Equal(g22,g21)
    c: Equal(g21,g20)
    c: Coincident(g9,g32)
    c: Equal(g6,g9)
    c: Equal(g14,g1)
    c: Equal(g1,g6)
    c: Coincident(g6,g31)
    c: Equal(g5,g10)
    c: Equal(g10,g13)
    c: Equal(g13,g2)
    c: Coincident(g8,g33)
FEATURE [PartDesign::Pocket] Pocket011
  BaseFeature = -> Pad006
  Direction = (0,0,-1)
  Length = 5
  Length2 = 5
  Profile = -> Sketch020
  ReferenceAxis = -> Sketch020 [N_Axis]
  Refine = true
  Suppressed = false
  Type = 2
FEATURE [Sketcher::SketchObject] Sketch021
  ArcFitTolerance = 0
  AttachmentSupport = -> [Pocket011]
  ExternalGeometry = -> [Pocket011]
  FullyConstrained = true
  MakeInternals = false
  MapMode = 5
  Placement = pos=(0,0,5) rot=(0,0,1;0rad)
  sketch-geometry (4):
    g0: Circle CenterX=36.5 CenterY=18.5 CenterZ=0 NormalX=0 NormalY=0 NormalZ=1 AngleXU=0 Radius=3
    g1: Circle CenterX=9 CenterY=5.25 CenterZ=0 NormalX=0 NormalY=0 NormalZ=1 AngleXU=0 Radius=3
    g2: Circle CenterX=64 CenterY=33.25 CenterZ=0 NormalX=0 NormalY=0 NormalZ=1 AngleXU=0 Radius=3
    g3: Circle CenterX=9 CenterY=33.25 CenterZ=0 NormalX=0 NormalY=0 NormalZ=1 AngleXU=0 Radius=3
  constraints (8):
    c: Coincident(g1,g-3)
    c: Coincident(g2,g-4)
    c: Diameter(g0) = 6
    c: Equal(g0,g2)
    c: Equal(g2,g3)
    c: Equal(g3,g1)
    c: Coincident(g3,g-5)
    c: Coincident(g0,g-6)
FEATURE [PartDesign::Pocket] Pocket012
  BaseFeature = -> Pocket011
  Direction = (0,0,-1)
  Length = 3.5
  Length2 = 5
  Profile = -> Sketch021
  ReferenceAxis = -> Sketch021 [N_Axis]
  Refine = true
  Suppressed = false
  Type = 0
FEATURE [PartDesign::Fillet] Fillet
  Base = -> Pocket012 [Edge10,Edge19,Edge7,Edge4]
  BaseFeature = -> Pocket012
  Radius = 1
  Refine = true
  SupportTransform = false
  Suppressed = false
  UseAllEdges = false
FEATURE [App::Link] base_top  label="BaseTopLeft"
  LinkPlacement = pos=(33.25,-64,0) rot=(0,0,1;1.5708rad)
  LinkedObject = -> Body007
  Placement = pos=(33.25,-64,0) rot=(0,0,1;1.5708rad)
FEATURE [Sketcher::SketchObject] Sketch023
  ArcFitTolerance = 0
  AttachmentSupport = -> [Fillet]
  ExternalGeometry = -> [Fillet]
  FullyConstrained = true
  MakeInternals = false
  MapMode = 5
  Placement = pos=(0,0,5) rot=(0,0,1;0rad)
  sketch-geometry (5):
    g0: LineSegment [constr] StartX=36.5 StartY=1 StartZ=0 EndX=36.5 EndY=4 EndZ=0
    g1: LineSegment StartX=36.5 StartY=4 StartZ=0 EndX=38.5 EndY=7 EndZ=0
    g2: LineSegment StartX=38.5 StartY=7 StartZ=0 EndX=34.5 EndY=7 EndZ=0
    g3: LineSegment StartX=34.5 StartY=7 StartZ=0 EndX=36.5 EndY=4 EndZ=0
    g4: LineSegment [constr] StartX=36.5 StartY=7 StartZ=0 EndX=36.5 EndY=4 EndZ=0
  constraints (13):
    c: Coincident(g1,g2)
    c: Horizontal(g2)
    c: Coincident(g2,g3)
    c: Coincident(g3,g1)
    c: DistanceX(g2,g2) = 4
    c: Vertical(g0)
    c: Coincident(g1,g0)
    c: DistanceY(g0,g0) = 3
    c: Symmetric(g-3,g-3,g0)
    c: Symmetric(g2,g2,g4)
    c: Coincident(g4,g0)
    c: Vertical(g4)
    c: DistanceY(g0,g1) = 3
FEATURE [PartDesign::Pocket] Pocket014
  BaseFeature = -> Fillet
  Direction = (0,0,-1)
  Length = 1
  Length2 = 5
  Profile = -> Sketch023
  ReferenceAxis = -> Sketch023 [N_Axis]
  Refine = true
  Suppressed = false
  Type = 0
FEATURE [PartDesign::Body] Body007  label="base-top"
  AllowCompound = false
  Group = -> [Sketch019,Pad006,Sketch020,Pocket011,Sketch021,Pocket012,Fillet,Sketch023,Pocket014]
  Origin = -> Origin005
  Tip = -> Pocket014
FEATURE [PartDesign::Pad] Pad003  label="cable"
  BaseFeature = -> Hole
  Direction = (1,0,0)
  Length = 10
  Length2 = 10
  Profile = -> Sketch005
  ReferenceAxis = -> Sketch005 [N_Axis]
  Refine = true
  Suppressed = false
  Type = 0
FEATURE [PartDesign::Body] Body001  label="stepper-motor"
  AllowCompound = false
  Group = -> [Sketch002,Pad001,Sketch003,Pad002,Sketch004,Hole,Sketch005,Pad003]
  Origin = -> Origin001
  Placement = pos=(0,0,41) rot=(0,0,1;0rad)
  Tip = -> Pad003
FEATURE [PartDesign::Pocket] Pocket006
  BaseFeature = -> Pocket005
  Direction = (0,0,1)
  Length = 4.5
  Length2 = 5
  Profile = -> Sketch014
  ReferenceAxis = -> Sketch014 [N_Axis]
  Refine = true
  Suppressed = false
  Type = 0
FEATURE [Sketcher::SketchObject] Sketch016
  ArcFitTolerance = 0
  AttachmentSupport = -> [Pocket006]
  ExternalGeometry = -> [Pocket006]
  FullyConstrained = true
  MakeInternals = false
  MapMode = 5
  Placement = pos=(0,18.5,0) rot=(1,0,0;1.5708rad)
  sketch-geometry (6):
    g0: LineSegment StartX=13.5 StartY=100 StartZ=0 EndX=13.5 EndY=10.5 EndZ=0
    g1: LineSegment StartX=13.5 StartY=10.5 StartZ=0 EndX=29.5 EndY=10.5 EndZ=0
    g2: LineSegment StartX=29.5 StartY=10.5 StartZ=0 EndX=29.5 EndY=100 EndZ=0
    g3: LineSegment [constr] StartX=3 StartY=100 StartZ=0 EndX=13.5 EndY=100 EndZ=0
    g4: LineSegment [constr] StartX=29.5 StartY=100 StartZ=0 EndX=40 EndY=100 EndZ=0
    g5: LineSegment StartX=13.5 StartY=100 StartZ=0 EndX=29.5 EndY=100 EndZ=0
  constraints (16):
    c: Coincident(g0,g1)
    c: Coincident(g1,g2)
    c: Vertical(g0)
    c: Vertical(g2)
    c: Horizontal(g1)
    c: Equal(g4,g3)
    c: DistanceX(g0,g2) = 16
    c: Coincident(g2,g4)
    c: Coincident(g3,g0)
    c: Horizontal(g3)
    c: Coincident(g0,g5)
    c: Coincident(g5,g2)
    c: Coincident(g3,g-3)
    c: Coincident(g4,g-3)
    c: PointOnObject(g2,g-3)
    c: PointOnObject(g1,g-4)
FEATURE [PartDesign::Pocket] Pocket008
  BaseFeature = -> Pocket006
  Direction = (0,1,-2e-16)
  Length = 14
  Length2 = 5
  Profile = -> Sketch016
  ReferenceAxis = -> Sketch016 [N_Axis]
  Refine = true
  Suppressed = false
  Type = 0
FEATURE [Sketcher::SketchObject] Sketch024
  ArcFitTolerance = 0
  AttachmentSupport = -> [Pocket008]
  ExternalGeometry = -> [Pocket008]
  FullyConstrained = true
  MakeInternals = false
  MapMode = 5
  Placement = pos=(0,-18.5,0) rot=(0,0.707107,0.707107;3.14159rad)
  sketch-geometry (6):
    g0: LineSegment StartX=-29.5 StartY=10.5 StartZ=0 EndX=-13.5 EndY=10.5 EndZ=0
    g1: LineSegment StartX=-13.5 StartY=10.5 StartZ=0 EndX=-13.5 EndY=100 EndZ=0
    g2: LineSegment StartX=-13.5 StartY=100 StartZ=0 EndX=-29.5 EndY=100 EndZ=0
    g3: LineSegment StartX=-29.5 StartY=100 StartZ=0 EndX=-29.5 EndY=10.5 EndZ=0
    g4: LineSegment [constr] StartX=-40 StartY=100 StartZ=0 EndX=-29.5 EndY=100 EndZ=0
    g5: LineSegment [constr] StartX=-13.5 StartY=100 StartZ=0 EndX=-3 EndY=100 EndZ=0
  constraints (16):
    c: Coincident(g2,g3)
    c: Coincident(g3,g0)
    c: Horizontal(g0)
    c: Horizontal(g2)
    c: Vertical(g1)
    c: Vertical(g3)
    c: PointOnObject(g1,g-3)
    c: DistanceX(g2,g2) = 16
    c: PointOnObject(g0,g-5)
    c: Coincident(g1,g2)
    c: Coincident(g1,g0)
    c: Coincident(g-3,g4)
    c: Coincident(g4,g2)
    c: Coincident(g1,g5)
    c: Coincident(g5,g-4)
    c: Equal(g5,g4)
FEATURE [PartDesign::Pocket] Pocket015
  BaseFeature = -> Pocket008
  Direction = (0,-1,2e-16)
  Length = 14
  Length2 = 5
  Profile = -> Sketch024
  ReferenceAxis = -> Sketch024 [N_Axis]
  Refine = true
  Suppressed = false
  Type = 0
FEATURE [Sketcher::SketchObject] Sketch018
  ArcFitTolerance = 0
  AttachmentSupport = -> [Pocket015]
  ExternalGeometry = -> [Pocket015]
  FullyConstrained = true
  MakeInternals = false
  MapMode = 5
  Placement = pos=(0,0,10.5) rot=(0,0,1;0rad)
  sketch-geometry (4):
    g0: LineSegment [constr] StartX=13.5 StartY=-18.5 StartZ=0 EndX=29.5 EndY=-32.5 EndZ=0
    g1: LineSegment [constr] StartX=13.5 StartY=18.5 StartZ=0 EndX=29.5 EndY=32.5 EndZ=0
    g2: Circle CenterX=21.5 CenterY=-25.5 CenterZ=0 NormalX=0 NormalY=0 NormalZ=1 AngleXU=0 Radius=3
    g3: Circle CenterX=21.5 CenterY=25.5 CenterZ=0 NormalX=0 NormalY=0 NormalZ=1 AngleXU=0 Radius=3
  constraints (8):
    c: Symmetric(g0,g0,g2)
    c: Diameter(g2) = 6
    c: Symmetric(g1,g1,g3)
    c: Equal(g3,g2)
    c: Coincident(g1,g-5)
    c: Coincident(g1,g-4)
    c: Coincident(g0,g-3)
    c: Coincident(g0,g-6)
FEATURE [PartDesign::Pocket] Pocket010
  BaseFeature = -> Pocket015
  Direction = (0,0,-1)
  Length = 5
  Length2 = 5
  Profile = -> Sketch018
  ReferenceAxis = -> Sketch018 [N_Axis]
  Refine = true
  Suppressed = false
  Type = 0
FEATURE [Sketcher::SketchObject] Sketch022
  ArcFitTolerance = 0
  AttachmentSupport = -> [Pocket010]
  ExternalGeometry = -> [Pocket010]
  FullyConstrained = true
  MakeInternals = false
  MapMode = 5
  Placement = pos=(0,0,100) rot=(0,0,1;0rad)
  sketch-geometry (8):
    g0: LineSegment [constr] StartX=13.5 StartY=18.5 StartZ=0 EndX=0 EndY=36.5 EndZ=0
    g1: LineSegment [constr] StartX=0 StartY=-36.5 StartZ=0 EndX=13.5 EndY=-18.5 EndZ=0
    g2: LineSegment [constr] StartX=29.5 StartY=-18.5 StartZ=0 EndX=40 EndY=-36.5 EndZ=0
    g3: LineSegment [constr] StartX=29.5 StartY=18.5 StartZ=0 EndX=40 EndY=36.5 EndZ=0
    g4: Circle CenterX=6.75 CenterY=27.5 CenterZ=0 NormalX=0 NormalY=0 NormalZ=1 AngleXU=0 Radius=1.3
    g5: Circle CenterX=34.75 CenterY=27.5 CenterZ=0 NormalX=0 NormalY=0 NormalZ=1 AngleXU=0 Radius=1.3
    g6: Circle CenterX=6.75 CenterY=-27.5 CenterZ=0 NormalX=0 NormalY=0 NormalZ=1 AngleXU=0 Radius=1.3
    g7: Circle CenterX=34.75 CenterY=-27.5 CenterZ=0 NormalX=0 NormalY=0 NormalZ=1 AngleXU=0 Radius=1.3
  constraints (16):
    c: Coincident(g1,g-8)
    c: Coincident(g1,g-9)
    c: Coincident(g2,g-9)
    c: Coincident(g2,g-10)
    c: Symmetric(g2,g2,g7)
    c: Symmetric(g1,g1,g6)
    c: Coincident(g0,g-12)
    c: Coincident(g0,g-13)
    c: Symmetric(g0,g0,g4)
    c: Symmetric(g3,g3,g5)
    c: Coincident(g3,g-11)
    c: Coincident(g3,g-13)
    c: Equal(g7,g6)
    c: Equal(g6,g4)
    c: Equal(g4,g5)
    c: Diameter(g4) = 2.6
FEATURE [PartDesign::Pocket] Pocket013
  BaseFeature = -> Pocket010
  Direction = (0,0,-1)
  Length = 10
  Length2 = 5
  Profile = -> Sketch022
  ReferenceAxis = -> Sketch022 [N_Axis]
  Refine = true
  Suppressed = false
  Type = 0
FEATURE [Sketcher::SketchObject] Sketch025
  ArcFitTolerance = 0
  AttachmentSupport = -> [XY_Plane006]
  FullyConstrained = true
  MakeInternals = false
  MapMode = 5
  sketch-geometry (8):
    g0: LineSegment [constr] StartX=0 StartY=0 StartZ=0 EndX=57 EndY=0 EndZ=0
    g1: LineSegment [constr] StartX=57 StartY=0 StartZ=0 EndX=57 EndY=57 EndZ=0
    g2: LineSegment [constr] StartX=57 StartY=57 StartZ=0 EndX=0 EndY=57 EndZ=0
    g3: LineSegment [constr] StartX=0 StartY=57 StartZ=0 EndX=0 EndY=0 EndZ=0
    g4: LineSegment StartX=0 StartY=28.5 StartZ=0 EndX=0 EndY=57 EndZ=0
    g5: LineSegment StartX=0 StartY=57 StartZ=0 EndX=57 EndY=57 EndZ=0
    g6: ArcOfCircle CenterX=28.5 CenterY=28.5 CenterZ=0 NormalX=0 NormalY=0 NormalZ=1 AngleXU=0 Radius=28.5 StartAngle=3.14159 EndAngle=6.28319
    g7: LineSegment StartX=57 StartY=57 StartZ=0 EndX=57 EndY=28.5 EndZ=0
  constraints (22):
    c: Coincident(g0,g1)
    c: Coincident(g1,g2)
    c: Coincident(g2,g3)
    c: Coincident(g3,g0)
    c: Horizontal(g0)
    c: Horizontal(g2)
    c: Vertical(g1)
    c: Coincident(g0,g-1)
    c: DistanceX(g2,g2) = 57
    c: Equal(g1,g2)
    c: Symmetric(g3,g3,g4)
    c: Coincident(g4,g2)
    c: Vertical(g4)
    c: Coincident(g4,g5)
    c: Horizontal(g5)
    c: Coincident(g6,g4)
    c: Tangent(g6,g0)
    c: Coincident(g5,g7)
    c: PointOnObject(g7,g1)
    c: Vertical(g7)
    c: Coincident(g6,g7)
    c: Equal(g7,g4)
FEATURE [PartDesign::Pad] Pad007
  Direction = (0,0,1)
  Length = 5
  Length2 = 10
  Profile = -> Sketch025
  ReferenceAxis = -> Sketch025 [N_Axis]
  Refine = true
  Suppressed = false
  Type = 0
FEATURE [Sketcher::SketchObject] Sketch026
  ArcFitTolerance = 0
  AttachmentSupport = -> [Pad007]
  ExternalGeometry = -> [Pad007]
  FullyConstrained = true
  MakeInternals = false
  MapMode = 5
  Placement = pos=(0,0,5) rot=(0,0,1;0rad)
  sketch-geometry (22):
    g0: ArcOfCircle [constr] CenterX=28.5 CenterY=28.5 CenterZ=0 NormalX=0 NormalY=0 NormalZ=1 AngleXU=0 Radius=27.5 StartAngle=1.8413 EndAngle=7.58348
    g1: LineSegment [constr] StartX=21.1515 StartY=55 StartZ=0 EndX=35.8485 EndY=55 EndZ=0
    g2: LineSegment [constr] StartX=28.5 StartY=55 StartZ=0 EndX=28.5 EndY=1 EndZ=0
    g3: GeomPoint [constr] X=28.5 Y=15 Z=0
    g4: GeomPoint [constr] X=28.5 Y=24 Z=0
    g5: LineSegment StartX=22.5 StartY=15 StartZ=0 EndX=34.5 EndY=15 EndZ=0
    g6: LineSegment StartX=12 StartY=24 StartZ=0 EndX=22.5 EndY=24 EndZ=0
    g7: LineSegment StartX=45 StartY=24 StartZ=0 EndX=45 EndY=44 EndZ=0
    g8: LineSegment StartX=45 StartY=57 StartZ=0 EndX=12 EndY=57 EndZ=0
    g9: LineSegment StartX=22.5 StartY=15 StartZ=0 EndX=22.5 EndY=24 EndZ=0
    g10: LineSegment StartX=34.5 StartY=15 StartZ=0 EndX=34.5 EndY=24 EndZ=0
    g11: LineSegment [constr] StartX=0 StartY=28.5 StartZ=0 EndX=56 EndY=28.5 EndZ=0
    g12: LineSegment StartX=34.5 StartY=24 StartZ=0 EndX=45 EndY=24 EndZ=0
    g13: LineSegment StartX=12 StartY=57 StartZ=0 EndX=-23.7172 EndY=57 EndZ=0
    g14: LineSegment StartX=45 StartY=57 StartZ=0 EndX=80.7172 EndY=57 EndZ=0
    g15: LineSegment StartX=-23.7172 StartY=57 StartZ=0 EndX=12 EndY=44 EndZ=0
    g16: LineSegment StartX=80.7172 StartY=57 StartZ=0 EndX=45 EndY=44 EndZ=0
    g17: LineSegment [constr] StartX=45 StartY=44 StartZ=0 EndX=12 EndY=44 EndZ=0
    g18: LineSegment StartX=12 StartY=44 StartZ=0 EndX=12 EndY=24 EndZ=0
    g19: LineSegment [constr] StartX=12 StartY=57 StartZ=0 EndX=12 EndY=44 EndZ=0
    g20: LineSegment [constr] StartX=45 StartY=44 StartZ=0 EndX=45 EndY=57 EndZ=0
    g21: GeomPoint [constr] X=0 Y=48.3676 Z=0
  constraints (63):
    c: Horizontal(g1)
    c: Symmetric(g1,g1,g2)
    c: PointOnObject(g2,g0)
    c: Vertical(g2)
    c: DistanceY(g2,g2) = 54
    c: Coincident(g0,g1)
    c: Coincident(g0,g1)
    c: Radius(g0) = 27.5
    c: PointOnObject(g3,g2)
    c: DistanceY(g2,g3) = 14
    c: PointOnObject(g4,g2)
    c: DistanceY(g2,g4) = 23
    c: Horizontal(g5)
    c: Coincident(g12,g7)
    c: Coincident(g18,g6)
    c: Horizontal(g6)
    c: Horizontal(g8)
    c: Vertical(g7)
    c: PointOnObject(g4,g6)
    c: Coincident(g5,g9)
    c: Vertical(g9)
    c: Coincident(g5,g10)
    c: PointOnObject(g10,g6)
    c: Vertical(g10)
    c: PointOnObject(g11,g-3)
    c: PointOnObject(g11,g0)
    c: Horizontal(g11)
    c: PointOnObject(g0,g11)
    c: Distance(g11,g7) = 11
    c: Coincident(g6,g9)
    c: Equal(g12,g6)
    c: Symmetric(g5,g5,g3)
    c: Horizontal(g12)
    c: Coincident(g12,g10)
    c: DistanceX(g5,g5) = 12
    c: Coincident(g8,g13)
    c: Horizontal(g13)
    c: Coincident(g8,g14)
    c: Horizontal(g14)
    c: Angle(g15,g13) = 0.349066
    c: DistanceY(g6,g15) = 20
    c: Coincident(g15,g13)
    c: Equal(g13,g14)
    c: Coincident(g14,g16)
    c: Coincident(g16,g17)
    c: Coincident(g17,g15)
    c: Horizontal(g17)
    c: Coincident(g7,g16)
    c: Coincident(g18,g15)
    c: Vertical(g18)
    c: Coincident(g8,g19)
    c: Coincident(g19,g15)
    c: Coincident(g7,g20)
    c: Coincident(g20,g8)
    c: Vertical(g20)
    c: Vertical(g19)
    c: Coincident(g0,g-4)
    c: PointOnObject(g8,g-5)
    c: PointOnObject(g21,g15)
    c: PointOnObject(g21,g-2)
    c: DistanceY(g9,g9) = 9
    c: DistanceX(g21,g15) = 12
    c: DistanceX(g17,g17) = 33
FEATURE [PartDesign::Pocket] Pocket016
  BaseFeature = -> Pad007
  Direction = (0,0,-1)
  Length = 5
  Length2 = 5
  Profile = -> Sketch026
  ReferenceAxis = -> Sketch026 [N_Axis]
  Refine = true
  Suppressed = false
  Type = 2
FEATURE [PartDesign::Pad] Pad008
  BaseFeature = -> Pad
  Direction = (0,0,-1)
  Length = 20
  Length2 = 10
  Profile = -> Sketch001
  ReferenceAxis = -> Sketch001 [N_Axis]
  Refine = true
  Suppressed = false
  Type = 0
FEATURE [App::Link] claw  label="Claw"
  LinkPlacement = pos=(-64.6617,33.7176,-96.1161) rot=(0,0,1;3.14159rad)
  LinkedObject = -> Body008
  Placement = pos=(-64.6617,33.7176,-96.1161) rot=(0,0,1;3.14159rad)
FEATURE [Sketcher::SketchObject] Sketch028
  ArcFitTolerance = 0
  AttachmentSupport = -> [Pocket016]
  ExternalGeometry = -> [Pocket016]
  FullyConstrained = true
  MakeInternals = false
  MapMode = 5
  Placement = pos=(0,0,5) rot=(0,0,1;0rad)
  sketch-geometry (7):
    g0: LineSegment [constr] StartX=37.5 StartY=7.5 StartZ=0 EndX=19.5 EndY=7.5 EndZ=0
    g1: GeomPoint X=28.5 Y=15 Z=0
    g2: GeomPoint X=28.5 Y=7.5 Z=0
    g3: LineSegment [constr] StartX=28.5 StartY=15 StartZ=0 EndX=28.5 EndY=7.5 EndZ=0
    g4: LineSegment [constr] StartX=28.5 StartY=0 StartZ=0 EndX=28.5 EndY=7.5 EndZ=0
    g5: Circle CenterX=19.5 CenterY=7.5 CenterZ=0 NormalX=0 NormalY=0 NormalZ=1 AngleXU=0 Radius=3.15
    g6: Circle CenterX=37.5 CenterY=7.5 CenterZ=0 NormalX=0 NormalY=0 NormalZ=1 AngleXU=0 Radius=3.15
  constraints (18):
    c: Horizontal(g0)
    c: Symmetric(g-3,g-3,g1)
    c: Symmetric(g0,g0,g2)
    c: Coincident(g3,g1)
    c: Coincident(g3,g2)
    c: Vertical(g3)
    c: PointOnObject(g4,g-1)
    c: Coincident(g4,g2)
    c: Vertical(g4)
    c: Equal(g4,g3)
    c: Coincident(g5,g0)
    c: Coincident(g6,g0)
    c: Diameter(g6) = 6.3
    c: Equal(g5,g6)
    c: DistanceX(g0,g0) = 18
    c: DistanceY(g0,g-3) = 7.5
    c: DistanceY(g0,g-4) = 40.8676
    c: DistanceY(g4,g0) = 7.5
FEATURE [PartDesign::Pocket] Pocket
  BaseFeature = -> Pocket016
  Direction = (0,0,-1)
  Length = 2
  Length2 = 5
  Profile = -> Sketch028
  ReferenceAxis = -> Sketch028 [N_Axis]
  Refine = true
  Suppressed = false
  Type = 0
FEATURE [Sketcher::SketchObject] Sketch029
  ArcFitTolerance = 0
  AttachmentSupport = -> [Pad008]
  ExternalGeometry = -> [Pad008]
  FullyConstrained = true
  MakeInternals = false
  MapMode = 5
  Placement = pos=(0,0,0) rot=(1,0,0;3.14159rad)
  sketch-geometry (16):
    g0: GeomPoint [constr] X=80 Y=-52.2941 Z=0
    g1: LineSegment [constr] StartX=80 StartY=-52.2941 StartZ=0 EndX=80 EndY=-59.7941 EndZ=0
    g2: LineSegment [constr] StartX=71 StartY=-59.7941 StartZ=0 EndX=89 EndY=-59.7941 EndZ=0
    g3: Circle CenterX=71 CenterY=-59.7941 CenterZ=0 NormalX=0 NormalY=0 NormalZ=1 AngleXU=0 Radius=4.15
    g4: Circle CenterX=89 CenterY=-59.7941 CenterZ=0 NormalX=0 NormalY=0 NormalZ=1 AngleXU=0 Radius=4.15
    g5: LineSegment [constr] StartX=51 StartY=-18.5625 StartZ=0 EndX=80 EndY=-29.1176 EndZ=0
    g6: LineSegment [constr] StartX=80 StartY=-29.1176 StartZ=0 EndX=109 EndY=-18.5625 EndZ=0
    g7: LineSegment [constr] StartX=51 StartY=-28.5625 StartZ=0 EndX=80 EndY=-39.1176 EndZ=0
    g8: LineSegment [constr] StartX=80 StartY=-39.1176 StartZ=0 EndX=109 EndY=-28.5625 EndZ=0
    g9: LineSegment [constr] StartX=64 StartY=-23.2941 StartZ=0 EndX=64 EndY=-43.2941 EndZ=0
    g10: LineSegment [constr] StartX=64 StartY=-43.2941 StartZ=0 EndX=74 EndY=-43.2941 EndZ=0
    g11: LineSegment [constr] StartX=74 StartY=-43.2941 StartZ=0 EndX=74 EndY=-52.2941 EndZ=0
    g12: LineSegment [constr] StartX=74 StartY=-52.2941 StartZ=0 EndX=86 EndY=-52.2941 EndZ=0
    g13: LineSegment [constr] StartX=86 StartY=-52.2941 StartZ=0 EndX=86 EndY=-43.2941 EndZ=0
    g14: LineSegment [constr] StartX=86 StartY=-43.2941 StartZ=0 EndX=96 EndY=-43.2941 EndZ=0
    g15: LineSegment [constr] StartX=96 StartY=-43.2941 StartZ=0 EndX=96 EndY=-23.2941 EndZ=0
  constraints (43):
    c: Coincident(g1,g0)
    c: Vertical(g1)
    c: Horizontal(g2)
    c: Symmetric(g2,g2,g1)
    c: Coincident(g3,g2)
    c: Coincident(g4,g2)
    c: Diameter(g4) = 8.3
    c: Equal(g4,g3)
    c: DistanceX(g2,g2) = 18
    c: Coincident(g5,g6)
    c: Angle(g5,g-1) = 0.349066
    c: Equal(g6,g5)
    c: Coincident(g7,g8)
    c: Parallel(g8,g6)
    c: Parallel(g7,g5)
    c: Coincident(g7,g-4)
    c: Vertical(g9)
    c: Coincident(g9,g10)
    c: Horizontal(g10)
    c: Coincident(g10,g11)
    c: Vertical(g11)
    c: Coincident(g11,g12)
    c: Horizontal(g12)
    c: Coincident(g12,g13)
    c: Coincident(g13,g14)
    c: Coincident(g14,g15)
    c: Vertical(g15)
    c: Horizontal(g14)
    c: Vertical(g13)
    c: Symmetric(g11,g12,g0)
    c: DistanceY(g15,g15) = 20
    c: Equal(g11,g13)
    c: Equal(g9,g15)
    c: Coincident(g5,g-3)
    c: DistanceY(g12,g14) = 9
    c: Equal(g10,g14)
    c: DistanceX(g12,g12) = 12
    c: DistanceY(g2,g12) = 7.5
    c: PointOnObject(g9,g5)
    c: PointOnObject(g15,g6)
    c: DistanceX(g9,g15) = 32
    c: Coincident(g8,g-5)
    c: Coincident(g6,g-5)
FEATURE [PartDesign::Pocket] Pocket017
  BaseFeature = -> Pad008
  Direction = (0,0,1)
  Length = 5
  Length2 = 5
  Profile = -> Sketch029
  ReferenceAxis = -> Sketch029 [N_Axis]
  Refine = true
  Suppressed = false
  Type = 2
FEATURE [Sketcher::SketchObject] Sketch030
  ArcFitTolerance = 0
  AttachmentSupport = -> [XY_Plane007]
  FullyConstrained = true
  MakeInternals = false
  MapMode = 5
  sketch-geometry (1):
    g0: Circle CenterX=0 CenterY=0 CenterZ=0 NormalX=0 NormalY=0 NormalZ=1 AngleXU=0 Radius=3
  constraints (2):
    c: Coincident(g0,g-1)
    c: Diameter(g0) = 6
FEATURE [PartDesign::Pad] Pad009
  Direction = (0,0,1)
  Length = 30
  Length2 = 10
  Profile = -> Sketch030
  ReferenceAxis = -> Sketch030 [N_Axis]
  Refine = true
  Suppressed = false
  Type = 0
FEATURE [PartDesign::Body] Body009  label="rod"
  AllowCompound = false
  Group = -> [Sketch030,Pad009]
  Origin = -> Origin007
  Tip = -> Pad009
FEATURE [App::Link] rod  label="rod001"
  LinkPlacement = pos=(-102.162,26.2176,-94.1161) rot=(0,0,1;0rad)
  LinkedObject = -> Body009
  Placement = pos=(-102.162,26.2176,-94.1161) rot=(0,0,1;0rad)
FEATURE [App::Link] rod001  label="rod002"
  LinkPlacement = pos=(-84.1617,26.2176,-93.1161) rot=(0,0,1;0rad)
  LinkedObject = -> Body009
  Placement = pos=(-84.1617,26.2176,-93.1161) rot=(0,0,1;0rad)
FEATURE [App::FeaturePython] GroundedJoint002  # Assembly grounded joint (typed FeaturePython)
  ObjectToGround = -> Body003
  Placement = pos=(-173.162,-33.5765,-80.1161) rot=(0,0,1;0rad)
FEATURE [Sketcher::SketchObject] Sketch031
  ArcFitTolerance = 0
  AttachmentSupport = -> [Pocket017]
  ExternalGeometry = -> [Pocket017]
  FullyConstrained = true
  MakeInternals = false
  MapMode = 5
  Placement = pos=(0,100,0) rot=(0,0.707107,0.707107;3.14159rad)
  sketch-geometry (6):
    g0: LineSegment StartX=-107.5 StartY=0 StartZ=0 EndX=-52.5 EndY=0 EndZ=0
    g1: LineSegment StartX=-52.5 StartY=0 StartZ=0 EndX=-52.5 EndY=10 EndZ=0
    g2: LineSegment StartX=-52.5 StartY=10 StartZ=0 EndX=-107.5 EndY=10 EndZ=0
    g3: LineSegment StartX=-107.5 StartY=10 StartZ=0 EndX=-107.5 EndY=0 EndZ=0
    g4: GeomPoint X=-80 Y=10 Z=0
    g5: GeomPoint X=-80 Y=10 Z=0
  constraints (13):
    c: Coincident(g0,g1)
    c: Coincident(g1,g2)
    c: Coincident(g2,g3)
    c: Coincident(g3,g0)
    c: Horizontal(g0)
    c: Horizontal(g2)
    c: Vertical(g1)
    c: Vertical(g3)
    c: PointOnObject(g0,g-1)
    c: Symmetric(g2,g2,g4)
    c: Symmetric(g-3,g-3,g5)
    c: Coincident(g4,g5)
    c: DistanceX(g2,g2) = 55
FEATURE [PartDesign::Pad] Pad010
  BaseFeature = -> Pocket017
  Direction = (0,1,-2e-16)
  Length = 20
  Length2 = 10
  Profile = -> Sketch031
  ReferenceAxis = -> Sketch031 [N_Axis]
  Refine = true
  Suppressed = false
  Type = 0
FEATURE [Sketcher::SketchObject] Sketch032
  ArcFitTolerance = 0
  AttachmentSupport = -> [Pad010]
  ExternalGeometry = -> [Pad010]
  FullyConstrained = true
  MakeInternals = false
  MapMode = 5
  Placement = pos=(0,0,-4e-16) rot=(1,0,0;3.14159rad)
  sketch-geometry (11):
    g0: Circle [constr] CenterX=80 CenterY=-95.2941 CenterZ=0 NormalX=0 NormalY=0 NormalZ=1 AngleXU=0 Radius=27.5
    g1: GeomPoint [constr] X=80 Y=-59.7941 Z=0
    g2: LineSegment [constr] StartX=80 StartY=-59.7941 StartZ=0 EndX=80 EndY=-95.2941 EndZ=0
    g3: LineSegment [constr] StartX=71 StartY=-67.7941 StartZ=0 EndX=89 EndY=-67.7941 EndZ=0
    g4: Circle CenterX=80 CenterY=-71.2941 CenterZ=0 NormalX=0 NormalY=0 NormalZ=1 AngleXU=0 Radius=3
    g5: Circle CenterX=101.25 CenterY=-106.449 CenterZ=0 NormalX=0 NormalY=0 NormalZ=1 AngleXU=0 Radius=3
    g6: Circle CenterX=58.75 CenterY=-106.449 CenterZ=0 NormalX=0 NormalY=0 NormalZ=1 AngleXU=0 Radius=3
    g7: LineSegment [constr] StartX=58.75 StartY=-106.449 StartZ=0 EndX=101.25 EndY=-106.449 EndZ=0
    g8: LineSegment [constr] StartX=80 StartY=-106.449 StartZ=0 EndX=80 EndY=-95.2941 EndZ=0
    g9: Circle [constr] CenterX=101.25 CenterY=-106.449 CenterZ=0 NormalX=0 NormalY=0 NormalZ=1 AngleXU=0 Radius=1.5
    g10: Circle [constr] CenterX=80 CenterY=-71.2941 CenterZ=0 NormalX=0 NormalY=0 NormalZ=1 AngleXU=0 Radius=1.5
  constraints (27):
    c: Diameter(g0) = 55
    c: Symmetric(g-4,g-3,g1)
    c: Coincident(g2,g1)
    c: Vertical(g2)
    c: Coincident(g0,g2)
    c: Horizontal(g3)
    c: Tangent(g3,g0)
    c: Distance(g-4,g3) = 8
    c: PointOnObject(g4,g2)
    c: Diameter(g4) = 6
    c: Equal(g6,g5)
    c: Equal(g5,g4)
    c: Horizontal(g6,g5)
    c: DistanceX(g6,g5) = 42.5
    c: Coincident(g7,g6)
    c: Coincident(g7,g5)
    c: Symmetric(g7,g7,g8)
    c: Coincident(g8,g0)
    c: Vertical(g8)
    c: Vertical(g3,g-3)
    c: Vertical(g3,g-4)
    c: Coincident(g9,g5)
    c: Diameter(g9) = 3
    c: Distance(g0,g9) = 2
    c: Coincident(g10,g4)
    c: Diameter(g10) = 3
    c: Distance(g10,g0) = 2
FEATURE [PartDesign::Pad] Pad011
  BaseFeature = -> Pad010
  Direction = (0,0,-1)
  Length = 2
  Length2 = 10
  Profile = -> Sketch032
  ReferenceAxis = -> Sketch032 [N_Axis]
  Refine = true
  Suppressed = false
  Type = 0
FEATURE [Sketcher::SketchObject] Sketch033
  ArcFitTolerance = 0
  AttachmentSupport = -> [Pad011]
  ExternalGeometry = -> [Pad011]
  FullyConstrained = true
  MakeInternals = false
  MapMode = 5
  Placement = pos=(0,0,-2) rot=(1,0,0;3.14159rad)
  sketch-geometry (3):
    g0: Circle CenterX=58.75 CenterY=-106.449 CenterZ=0 NormalX=0 NormalY=0 NormalZ=1 AngleXU=0 Radius=1.85
    g1: Circle CenterX=101.25 CenterY=-106.449 CenterZ=0 NormalX=0 NormalY=0 NormalZ=1 AngleXU=0 Radius=1.85
    g2: Circle CenterX=80 CenterY=-71.2941 CenterZ=0 NormalX=0 NormalY=0 NormalZ=1 AngleXU=0 Radius=1.85
  constraints (6):
    c: Coincident(g0,g-4)
    c: Coincident(g1,g-5)
    c: Coincident(g2,g-3)
    c: Equal(g2,g0)
    c: Equal(g0,g1)
    c: Diameter(g2) = 3.7
FEATURE [PartDesign::Pocket] Pocket018
  BaseFeature = -> Pad011
  Direction = (0,0,1)
  Length = 5
  Length2 = 5
  Profile = -> Sketch033
  ReferenceAxis = -> Sketch033 [N_Axis]
  Refine = true
  Suppressed = false
  Type = 1
FEATURE [Sketcher::SketchObject] Sketch034
  ArcFitTolerance = 0
  AttachmentSupport = -> [Pocket018]
  ExternalGeometry = -> [Pocket018]
  FullyConstrained = true
  MakeInternals = false
  MapMode = 5
  Placement = pos=(0,0,10) rot=(0,0,1;0rad)
  sketch-geometry (3):
    g0: Circle CenterX=58.75 CenterY=106.449 CenterZ=0 NormalX=0 NormalY=0 NormalZ=1 AngleXU=0 Radius=3.25
    g1: Circle CenterX=101.25 CenterY=106.449 CenterZ=0 NormalX=0 NormalY=0 NormalZ=1 AngleXU=0 Radius=3.25
    g2: Circle CenterX=80 CenterY=71.2941 CenterZ=0 NormalX=0 NormalY=0 NormalZ=1 AngleXU=0 Radius=3.25
  constraints (6):
    c: Coincident(g0,g-3)
    c: Equal(g2,g0)
    c: Equal(g0,g1)
    c: Diameter(g0) = 6.5
    c: Coincident(g1,g-5)
    c: Coincident(g2,g-4)
FEATURE [PartDesign::Pocket] Pocket019
  BaseFeature = -> Pocket018
  Direction = (0,0,-1)
  Length = 5
  Length2 = 5
  Profile = -> Sketch034
  ReferenceAxis = -> Sketch034 [N_Axis]
  Refine = true
  Suppressed = false
  Type = 0
FEATURE [PartDesign::Chamfer] Chamfer
  Angle = 45
  Base = -> Pocket013 [Edge75,Edge82,Edge87,Edge56]
  BaseFeature = -> Pocket013
  ChamferType = 0
  FlipDirection = false
  Refine = true
  Size = 5
  Size2 = 1
  SupportTransform = false
  Suppressed = false
  UseAllEdges = false
FEATURE [PartDesign::Body] Body006  label="base"
  AllowCompound = false
  Group = -> [Sketch007,Pad005,Sketch008,Pocket001,Sketch009,Pocket002,Sketch011,Pocket003,Sketch012,Pocket004,Sketch013,Pocket005,Sketch014,Pocket006,Sketch016,Pocket008,Sketch024,Pocket015,Sketch018,Pocket010,Sketch022,Pocket013,Chamfer]
  Origin = -> Origin004
  Tip = -> Chamfer
FEATURE [Sketcher::SketchObject] Sketch035
  ArcFitTolerance = 0
  AttachmentSupport = -> [Pocket019]
  ExternalGeometry = -> [Pocket019]
  FullyConstrained = true
  MakeInternals = false
  MapMode = 5
  Placement = pos=(0,0,-4e-16) rot=(1,0,0;3.14159rad)
  sketch-geometry (12):
    g0: LineSegment StartX=145 StartY=-22.5 StartZ=0 EndX=145 EndY=-57.5 EndZ=0
    g1: LineSegment StartX=145 StartY=-57.5 StartZ=0 EndX=160 EndY=-57.5 EndZ=0
    g2: LineSegment StartX=160 StartY=-57.5 StartZ=0 EndX=160 EndY=-22.5 EndZ=0
    g3: LineSegment StartX=160 StartY=-22.5 StartZ=0 EndX=145 EndY=-22.5 EndZ=0
    g4: GeomPoint X=80 Y=0 Z=0
    g5: LineSegment [constr] StartX=80 StartY=0 StartZ=0 EndX=80 EndY=-100 EndZ=0
    g6: LineSegment StartX=0 StartY=-22.5 StartZ=0 EndX=15 EndY=-22.5 EndZ=0
    g7: LineSegment StartX=15 StartY=-22.5 StartZ=0 EndX=15 EndY=-57.5 EndZ=0
    g8: LineSegment StartX=15 StartY=-57.5 StartZ=0 EndX=0 EndY=-57.5 EndZ=0
    g9: LineSegment StartX=0 StartY=-57.5 StartZ=0 EndX=0 EndY=-22.5 EndZ=0
    g10: LineSegment [constr] StartX=0 StartY=0 StartZ=0 EndX=0 EndY=-22.5 EndZ=0
    g11: LineSegment [constr] StartX=160 StartY=-22.5 StartZ=0 EndX=160 EndY=0 EndZ=0
  constraints (31):
    c: Coincident(g0,g1)
    c: Coincident(g1,g2)
    c: Coincident(g2,g3)
    c: Coincident(g3,g0)
    c: Vertical(g0)
    c: Vertical(g2)
    c: Horizontal(g1)
    c: Horizontal(g3)
    c: DistanceY(g0,g0) = 35
    c: DistanceX(g3,g3) = 15
    c: PointOnObject(g2,g-3)
    c: DistanceY(g2,g-4) = 22.5
    c: Symmetric(g-4,g-4,g4)
    c: Coincident(g5,g4)
    c: Coincident(g7,g8)
    c: Coincident(g8,g9)
    c: Coincident(g9,g6)
    c: Coincident(g6,g7)
    c: Coincident(g-1,g10)
    c: Coincident(g10,g6)
    c: Vertical(g10)
    c: Coincident(g2,g11)
    c: Coincident(g11,g-4)
    c: Equal(g11,g10)
    c: Equal(g1,g8)
    c: Equal(g7,g0)
    c: Vertical(g7)
    c: Horizontal(g8)
    c: Horizontal(g6)
    c: Vertical(g9)
    c: Symmetric(g-6,g-5,g5)
FEATURE [PartDesign::Pocket] Pocket020
  BaseFeature = -> Pocket019
  Direction = (0,0,1)
  Length = 5.3
  Length2 = 5
  Profile = -> Sketch035
  ReferenceAxis = -> Sketch035 [N_Axis]
  Refine = true
  Suppressed = false
  Type = 0
FEATURE [Sketcher::SketchObject] Sketch036
  ArcFitTolerance = 0
  AttachmentSupport = -> [Pocket020]
  ExternalGeometry = -> [Pocket020]
  FullyConstrained = true
  MakeInternals = false
  MapMode = 5
  Placement = pos=(0,0,5.3) rot=(1,0,0;3.14159rad)
  sketch-geometry (12):
    g0: GeomPoint [constr] X=152.5 Y=-22.5 Z=0
    g1: GeomPoint [constr] X=152.5 Y=-57.5 Z=0
    g2: GeomPoint [constr] X=160 Y=-40 Z=0
    g3: GeomPoint [constr] X=145 Y=-40 Z=0
    g4: LineSegment [constr] StartX=145 StartY=-40 StartZ=0 EndX=160 EndY=-40 EndZ=0
    g5: GeomPoint [constr] X=152.5 Y=-40 Z=0
    g6: Circle CenterX=152.5 CenterY=-31.25 CenterZ=0 NormalX=0 NormalY=0 NormalZ=1 AngleXU=0 Radius=1.3
    g7: Circle CenterX=152.5 CenterY=-48.75 CenterZ=0 NormalX=0 NormalY=0 NormalZ=1 AngleXU=0 Radius=1.3
    g8: LineSegment [constr] StartX=7.5 StartY=-22.5 StartZ=0 EndX=7.5 EndY=-57.5 EndZ=0
    g9: GeomPoint [constr] X=7.5 Y=-40 Z=0
    g10: Circle CenterX=7.5 CenterY=-31.25 CenterZ=0 NormalX=0 NormalY=0 NormalZ=1 AngleXU=0 Radius=1.3
    g11: Circle CenterX=7.5 CenterY=-48.75 CenterZ=0 NormalX=0 NormalY=0 NormalZ=1 AngleXU=0 Radius=1.3
  constraints (18):
    c: Symmetric(g-3,g-3,g0)
    c: Symmetric(g-4,g-3,g2)
    c: Symmetric(g-4,g-4,g1)
    c: Symmetric(g-3,g-4,g3)
    c: Coincident(g4,g3)
    c: Coincident(g4,g2)
    c: Symmetric(g4,g4,g5)
    c: Symmetric(g5,g1,g7)
    c: Symmetric(g5,g0,g6)
    c: Equal(g7,g6)
    c: Diameter(g6) = 2.6
    c: Symmetric(g-5,g-5,g8)
    c: Symmetric(g-7,g-7,g8)
    c: Symmetric(g8,g8,g9)
    c: Symmetric(g9,g8,g11)
    c: Symmetric(g9,g8,g10)
    c: Equal(g10,g11)
    c: Equal(g6,g10)
FEATURE [PartDesign::Pocket] Pocket021
  BaseFeature = -> Pocket020
  Direction = (0,0,1)
  Length = 5
  Length2 = 5
  Profile = -> Sketch036
  ReferenceAxis = -> Sketch036 [N_Axis]
  Refine = true
  Suppressed = false
  Type = 1
FEATURE [PartDesign::Body] Body  label="beam"
  AllowCompound = false
  Group = -> [Sketch,Pad,Sketch001,Pad008,Sketch029,Pocket017,Sketch031,Pad010,Sketch032,Pad011,Sketch033,Pocket018,Sketch034,Pocket019,Sketch035,Pocket020,Sketch036,Pocket021]
  Origin = -> Origin
  Tip = -> Pocket021
FEATURE [App::FeaturePython] Slider002  # Assembly joint (typed FeaturePython)
  Activated = true
  AngleMax = 0
  AngleMin = 0
  Detach1 = false
  Detach2 = false
  Distance = 0
  Distance2 = 0
  EnableAngleMax = false
  EnableAngleMin = false
  EnableLengthMax = false
  EnableLengthMin = false
  EnableLimits = false
  JointType = 3 (Slider)
  LengthMax = 0
  LengthMin = 0
  Offset1 = pos=(0,0,8) rot=(0,0,1;0rad)
  Placement1 = pos=(0,0,23) rot=(0,0,1;0rad)
  Placement2 = pos=(89,59.7941,10) rot=(1,0,0;3.14159rad)
  Reference1 = -> Assembly [rod001.Face1,rod001.Face1]
  Reference2 = -> Assembly [Body003.Edge57,Body003.Edge57]
FEATURE [App::FeaturePython] Joint  label="Slider003"  # Assembly joint (typed FeaturePython)
  Activated = true
  AngleMax = 0
  AngleMin = 0
  Detach1 = false
  Detach2 = false
  Distance = 0
  Distance2 = 0
  EnableAngleMax = false
  EnableAngleMin = false
  EnableLengthMax = false
  EnableLengthMin = false
  JointType = 3 (Slider)
  LengthMax = 0
  LengthMin = 0
  Offset1 = pos=(0,0,4) rot=(0,0,1;0rad)
  Placement1 = pos=(0,0,19) rot=(0,0,1;0rad)
  Placement2 = pos=(71,59.7941,5) rot=(1,0,0;3.14159rad)
  Reference1 = -> Assembly [rod.Face1,rod.Face1]
  Reference2 = -> Assembly [Body003.Face28,Body003.Face28]
FEATURE [App::FeaturePython] Joint001  label="Fixed002"  # Assembly joint (typed FeaturePython)
  Activated = true
  AngleMax = 0
  AngleMin = 0
  Detach1 = false
  Detach2 = false
  Distance = 0
  Distance2 = 0
  EnableAngleMax = false
  EnableAngleMin = false
  EnableLengthMax = false
  EnableLengthMin = false
  JointType = 0 (Fixed)
  LengthMax = 0
  LengthMin = 0
  Offset2 = pos=(0,0,0) rot=(0,0,1;3.14159rad)
  Placement2 = pos=(19.5,7.5,3) rot=(0,0,1;3.14159rad)
  Reference1 = -> Assembly [rod001.Edge2,rod001.Edge2]
  Reference2 = -> Assembly [claw.Face19,claw.Face19]
FEATURE [App::FeaturePython] Joint002  label="Fixed"  # Assembly joint (typed FeaturePython)
  Activated = true
  AngleMax = 0
  AngleMin = 0
  Detach1 = false
  Detach2 = false
  Distance = 0
  Distance2 = 0
  EnableAngleMax = false
  EnableAngleMin = false
  EnableLengthMax = false
  EnableLengthMin = false
  JointType = 0 (Fixed)
  LengthMax = 0
  LengthMin = 0
  Offset2 = pos=(0,0,0) rot=(0,0,1;1.5708rad)
  Placement1 = pos=(64,33.25,0) rot=(0,0,1;0rad)
  Placement2 = pos=(213.899,-29.7686,94.7418) rot=(0,0,1;1.5708rad)
  Reference1 = -> Assembly [base_top.Edge19,base_top.Edge19]
  Reference2 = -> Assembly [Body004.?Edge23,Body004.?Edge23]
FEATURE [App::Link] base_top001  label="BaseTopRight"
  LinkPlacement = pos=(-5.25,64,-1.79e-14) rot=(0,0,1;4.71239rad)
  LinkedObject = -> Body007
  Placement = pos=(-5.25,64,-1.79e-14) rot=(0,0,1;4.71239rad)
FEATURE [App::FeaturePython] Joint003  label="Fixed003"  # Assembly joint (typed FeaturePython)
  Activated = true
  AngleMax = 0
  AngleMin = 0
  Detach1 = false
  Detach2 = false
  Distance = 0
  Distance2 = 0
  EnableAngleMax = false
  EnableAngleMin = false
  EnableLengthMax = false
  EnableLengthMin = false
  JointType = 0 (Fixed)
  LengthMax = 0
  LengthMin = 0
  Offset2 = pos=(0,0,0) rot=(0,0,1;1.5708rad)
  Placement1 = pos=(64,5.25,0) rot=(0,0,1;0rad)
  Placement2 = pos=(67.4324,29.1063,94.7418) rot=(0,0,-1;1.5708rad)
  Reference1 = -> Assembly [base_top001.Edge15,base_top001.Edge15]
  Reference2 = -> Assembly [Body005.?Edge24,Body005.?Edge24]
FEATURE [Sketcher::SketchObject] Sketch037
  ArcFitTolerance = 0
  AttachmentSupport = -> [XY_Plane008]
  FullyConstrained = true
  MakeInternals = false
  MapMode = 5
  sketch-geometry (4):
    g0: LineSegment StartX=0 StartY=0 StartZ=0 EndX=0 EndY=15 EndZ=0
    g1: LineSegment StartX=0 StartY=15 StartZ=0 EndX=30 EndY=15 EndZ=0
    g2: LineSegment StartX=30 StartY=15 StartZ=0 EndX=30 EndY=-5.44826e-11 EndZ=0
    g3: LineSegment StartX=0 StartY=0 StartZ=0 EndX=30 EndY=-5.44826e-11 EndZ=0
  constraints (11):
    c: Vertical(g0)
    c: Coincident(g0,g1)
    c: Horizontal(g1)
    c: Coincident(g1,g2)
    c: Vertical(g2)
    c: Equal(g2,g0)
    c: Coincident(g0,g-1)
    c: DistanceX(g1,g1) = 30
    c: Coincident(g0,g3)
    c: Coincident(g3,g2)
    c: DistanceY(g2,g2) = 15
FEATURE [PartDesign::Pad] Pad012
  Direction = (0,0,1)
  Length = 5
  Length2 = 10
  Profile = -> Sketch037
  ReferenceAxis = -> Sketch037 [N_Axis]
  Refine = true
  Suppressed = false
  Type = 0
FEATURE [Sketcher::SketchObject] Sketch039
  ArcFitTolerance = 0
  ExternalGeometry = -> [Pad012]
  FullyConstrained = true
  MakeInternals = false
  MapMode = 5
  Placement = pos=(0,0,5) rot=(0,0,1;0rad)
  sketch-geometry (7):
    g0: LineSegment [constr] StartX=24 StartY=7.5 StartZ=0 EndX=6 EndY=7.5 EndZ=0
    g1: GeomPoint X=15 Y=15 Z=0
    g2: GeomPoint X=15 Y=7.5 Z=0
    g3: LineSegment [constr] StartX=15 StartY=15 StartZ=0 EndX=15 EndY=7.5 EndZ=0
    g4: LineSegment [constr] StartX=15 StartY=0 StartZ=0 EndX=15 EndY=7.5 EndZ=0
    g5: Circle CenterX=6 CenterY=7.5 CenterZ=0 NormalX=0 NormalY=0 NormalZ=1 AngleXU=0 Radius=3.15
    g6: Circle CenterX=24 CenterY=7.5 CenterZ=0 NormalX=0 NormalY=0 NormalZ=1 AngleXU=0 Radius=3.15
  constraints (16):
    c: Horizontal(g0)
    c: Symmetric(g0,g0,g2)
    c: Coincident(g3,g1)
    c: Coincident(g3,g2)
    c: Vertical(g3)
    c: PointOnObject(g4,g-1)
    c: Coincident(g4,g2)
    c: Vertical(g4)
    c: Equal(g4,g3)
    c: Coincident(g5,g0)
    c: Coincident(g6,g0)
    c: Diameter(g6) = 6.3
    c: Equal(g5,g6)
    c: DistanceX(g0,g0) = 18
    c: DistanceY(g4,g0) = 7.5
    c: Symmetric(g-3,g-3,g1)
FEATURE [PartDesign::Pocket] Pocket022
  BaseFeature = -> Pad012
  Direction = (0,0,-1)
  Length = 2
  Length2 = 5
  Profile = -> Sketch039
  ReferenceAxis = -> Sketch039 [N_Axis]
  Refine = true
  Suppressed = false
  Type = 0
FEATURE [Sketcher::SketchObject] Sketch040
  ArcFitTolerance = 1e-06
  AttachmentSupport = -> [Pocket022]
  ExternalGeometry = -> [Pocket022]
  FullyConstrained = true
  MakeInternals = false
  MapMode = 5
  Placement = pos=(0,0,3) rot=(0,0,1;0rad)
  sketch-geometry (2):
    g0: Circle CenterX=24 CenterY=7.5 CenterZ=0 NormalX=0 NormalY=0 NormalZ=1 AngleXU=0 Radius=1.3
    g1: Circle CenterX=6 CenterY=7.5 CenterZ=0 NormalX=0 NormalY=0 NormalZ=1 AngleXU=0 Radius=1.3
  constraints (4):
    c: Coincident(g0,g-3)
    c: Coincident(g1,g-4)
    c: Equal(g0,g1)
    c: Diameter(g0) = 2.6
FEATURE [PartDesign::Pocket] Pocket023
  BaseFeature = -> Pocket022
  Direction = (0,0,-1)
  Length = 5
  Length2 = 5
  Profile = -> Sketch040
  ReferenceAxis = -> Sketch040 [N_Axis]
  Refine = true
  Suppressed = false
  Type = 2
FEATURE [Sketcher::SketchObject] Sketch041
  ArcFitTolerance = 1e-06
  AttachmentSupport = -> [Pocket]
  ExternalGeometry = -> [Pocket]
  FullyConstrained = true
  MakeInternals = false
  MapMode = 5
  Placement = pos=(0,0,3) rot=(0,0,1;0rad)
  sketch-geometry (2):
    g0: Circle CenterX=19.5 CenterY=7.5 CenterZ=0 NormalX=0 NormalY=0 NormalZ=1 AngleXU=0 Radius=1.3
    g1: Circle CenterX=37.5 CenterY=7.5 CenterZ=0 NormalX=0 NormalY=0 NormalZ=1 AngleXU=0 Radius=1.3
  constraints (4):
    c: Coincident(g0,g-4)
    c: Coincident(g1,g-3)
    c: Equal(g1,g0)
    c: Diameter(g0) = 2.6
FEATURE [PartDesign::Pocket] Pocket024
  BaseFeature = -> Pocket
  Direction = (0,0,-1)
  Length = 5
  Length2 = 5
  Profile = -> Sketch041
  ReferenceAxis = -> Sketch041 [N_Axis]
  Refine = true
  Suppressed = false
  Type = 2
FEATURE [PartDesign::Body] Body008  label="claw"
  AllowCompound = false
  Group = -> [Sketch025,Pad007,Sketch026,Pocket016,Sketch028,Pocket,Sketch041,Pocket024]
  Origin = -> Origin006
  Tip = -> Pocket024
FEATURE [App::Link] claw_holder  label="claw-holder001"
  LinkPlacement = pos=(-108.162,33.7176,-61.1161) rot=(1,0,0;3.14159rad)
  LinkedObject = -> Body010
  Placement = pos=(-108.162,33.7176,-61.1161) rot=(1,0,0;3.14159rad)
FEATURE [App::FeaturePython] Joint004  label="Fixed004"  # Assembly joint (typed FeaturePython)
  Activated = true
  AngleMax = 0
  AngleMin = 0
  Detach1 = false
  Detach2 = false
  Distance = 0
  Distance2 = 0
  EnableAngleMax = false
  EnableAngleMin = false
  EnableLengthMax = false
  EnableLengthMin = false
  JointType = 0 (Fixed)
  LengthMax = 0
  LengthMin = 0
  Offset2 = pos=(0,0,0) rot=(1,0,0;3.14159rad)
  Placement1 = pos=(6,7.5,3) rot=(0,0,1;0rad)
  Placement2 = pos=(0,0,30) rot=(1,0,0;3.14159rad)
  Reference1 = -> Assembly [claw_holder.Edge30,claw_holder.Edge30]
  Reference2 = -> Assembly [rod.Face3,rod.Face3]
FEATURE [Assembly::JointGroup] Joints
  Group = -> [GroundedJoint001,GroundedJoint,GroundedJoint002,Slider002,Joint,Joint001,Joint002,Joint003,Joint004]
FEATURE [Assembly::AssemblyObject] Assembly
  Group = -> [Joints,Body003,Body004,Body005,GroundedJoint001,GroundedJoint,base_top,claw,rod,rod001,GroundedJoint002,Slider002,Joint,Joint001,Joint002,base_top001,Joint003,claw_holder,Joint004]
  Origin = -> Origin003
  Type = Assembly
FEATURE [PartDesign::Fillet] Fillet001
  Base = -> Pocket023 [Edge5,Edge1,Edge2,Edge8]
  BaseFeature = -> Pocket023
  Radius = 3
  Refine = true
  SupportTransform = false
  Suppressed = false
  UseAllEdges = false
FEATURE [PartDesign::Body] Body010  label="claw-holder"
  AllowCompound = false
  Group = -> [Sketch037,Pad012,Sketch039,Pocket022,Sketch040,Pocket023,Fillet001]
  Origin = -> Origin008
  Tip = -> Fillet001
